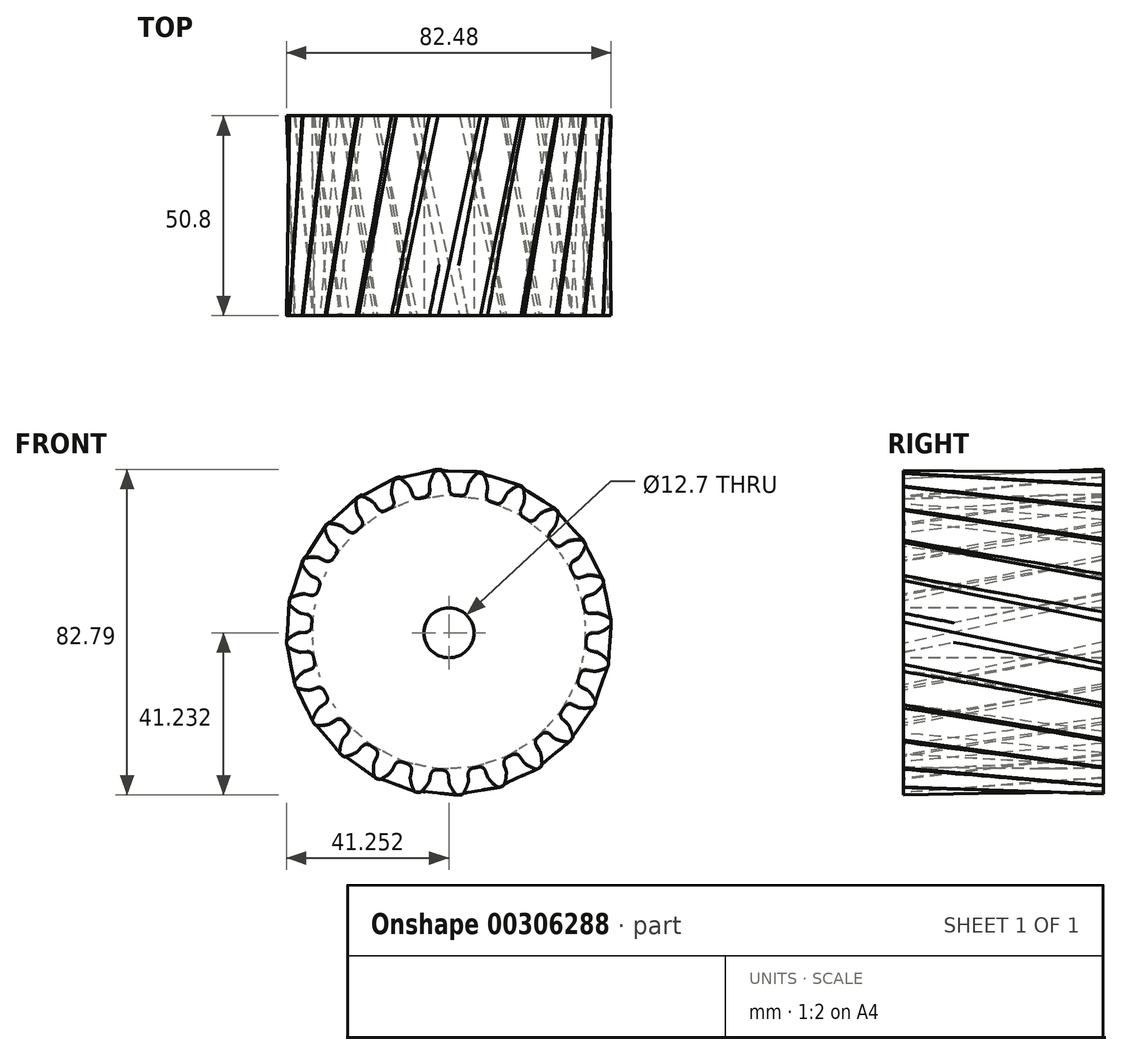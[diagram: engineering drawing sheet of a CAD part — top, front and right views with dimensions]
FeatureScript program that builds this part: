
annotation { "Feature Type Name" : "Feature", "Feature Type Description" : "" }
export const myFeature = defineFeature(function(context is Context, id is Id, definition is map)
    precondition{}
    {
        {
            var Q0;
            Q0=qCreatedBy(makeId("Front.planeOp"),FACE);
            var sketch = newSketch(context, id + "F0", { "sketchPlane" : qUnion([Q0])});
            skArc(sketch, "E0", {"start": v(-6.16, 34.38) * mm, "mid": v(-6.81, 34.25) * mm, "end": v(-7.46, 34.12) * mm});
            skArc(sketch, "E1.trimOffspring", {"start": v(-0.1, 38.36) * mm, "mid": v(-0.85, 39.78) * mm, "end": v(-1.82, 41.06) * mm});
            skLineSegment(sketch, "E2", {"start": v(0.02, 37.85) * mm, "end": v(0.11, 36.37) * mm});
            skLineSegment(sketch, "E3", {"start": v(-2.2, 41.23) * mm, "end": v(-2.7, 41.23) * mm});
            skLineSegment(sketch, "E4.MirrorCS", {"start": v(-3.2, 41.16) * mm, "end": v(-2.7, 41.23) * mm});
            skArc(sketch, "E5.MirrorCS", {"start": v(-4.9, 38.04) * mm, "mid": v(-4.35, 39.55) * mm, "end": v(-3.56, 40.95) * mm});
            skLineSegment(sketch, "E6.MirrorCS", {"start": v(-4.96, 37.52) * mm, "end": v(-4.86, 36.04) * mm});
            skPoint(sketch, "E7.orphan", {"position": v(0.33, 33.11) * mm});
            skPoint(sketch, "E8.orphan", {"position": v(-4.65, 32.79) * mm});
            skPoint(sketch, "E9.visualSharp", {"position": v(0.2, 34.92) * mm});
            skArc(sketch, "E9.filletArc", {"start": v(0.11, 36.37) * mm, "mid": v(0.59, 35.34) * mm, "end": v(1.62, 34.89) * mm});
            skPoint(sketch, "E10.visualSharp", {"position": v(-4.76, 34.6) * mm});
            skArc(sketch, "E10.filletArc", {"start": v(-6.16, 34.38) * mm, "mid": v(-5.2, 34.96) * mm, "end": v(-4.86, 36.04) * mm});
            skPoint(sketch, "E11.visualSharp", {"position": v(-3.43, 41.13) * mm});
            skArc(sketch, "E11.filletArc", {"start": v(-3.2, 41.16) * mm, "mid": v(-3.4, 41.1) * mm, "end": v(-3.56, 40.95) * mm});
            skPoint(sketch, "E12.visualSharp", {"position": v(-1.97, 41.23) * mm});
            skArc(sketch, "E12.filletArc", {"start": v(-1.82, 41.06) * mm, "mid": v(-1.99, 41.18) * mm, "end": v(-2.2, 41.23) * mm});
            skPoint(sketch, "E13.visualSharp", {"position": v(-4.97, 37.77) * mm});
            skArc(sketch, "E13.filletArc", {"start": v(-4.9, 38.04) * mm, "mid": v(-4.95, 37.78) * mm, "end": v(-4.96, 37.52) * mm});
            skPoint(sketch, "E14.visualSharp", {"position": v(0, 38.1) * mm});
            skArc(sketch, "E14.filletArc", {"start": v(0.02, 37.85) * mm, "mid": v(-0.02, 38.1) * mm, "end": v(-0.1, 38.36) * mm});
            skArc(sketch, "E15.1.0", {"start": v(-9.3, 35.16) * mm, "mid": v(-8.58, 34.29) * mm, "end": v(-7.46, 34.12) * mm});
            skArc(sketch, "E15.1.1", {"start": v(-14.85, 31.61) * mm, "mid": v(-14.07, 32.43) * mm, "end": v(-14.02, 33.56) * mm});
            skLineSegment(sketch, "E15.1.2", {"start": v(-9.78, 36.56) * mm, "end": v(-9.3, 35.16) * mm});
            skLineSegment(sketch, "E15.1.3", {"start": v(-14.5, 34.96) * mm, "end": v(-14.02, 33.56) * mm});
            skPoint(sketch, "E15.1.4", {"position": v(-12.58, 39.31) * mm});
            skPoint(sketch, "E15.1.5", {"position": v(-13.96, 38.84) * mm});
            skArc(sketch, "E15.1.6", {"start": v(-14.58, 35.48) * mm, "mid": v(-14.44, 37.08) * mm, "end": v(-14.03, 38.63) * mm});
            skPoint(sketch, "E15.1.7", {"position": v(-14.58, 35.2) * mm});
            skPoint(sketch, "E15.1.8", {"position": v(-9.86, 36.8) * mm});
            skArc(sketch, "E15.1.9", {"start": v(-10.03, 37.02) * mm, "mid": v(-11.11, 38.2) * mm, "end": v(-12.38, 39.2) * mm});
            skLineSegment(sketch, "E15.1.10", {"start": v(-12.79, 39.26) * mm, "end": v(-13.28, 39.12) * mm});
            skLineSegment(sketch, "E15.1.11", {"start": v(-13.75, 38.93) * mm, "end": v(-13.28, 39.12) * mm});
            skArc(sketch, "E15.1.12", {"start": v(-9.78, 36.56) * mm, "mid": v(-9.88, 36.8) * mm, "end": v(-10.03, 37.02) * mm});
            skArc(sketch, "E15.1.13", {"start": v(-13.75, 38.93) * mm, "mid": v(-13.92, 38.8) * mm, "end": v(-14.03, 38.63) * mm});
            skArc(sketch, "E15.1.14", {"start": v(-14.58, 35.48) * mm, "mid": v(-14.56, 35.22) * mm, "end": v(-14.5, 34.96) * mm});
            skArc(sketch, "E15.1.15", {"start": v(-12.38, 39.2) * mm, "mid": v(-12.58, 39.27) * mm, "end": v(-12.79, 39.26) * mm});
            skArc(sketch, "E15.2.0", {"start": v(-18.09, 31.55) * mm, "mid": v(-17.16, 30.9) * mm, "end": v(-16.04, 31.03) * mm});
            skArc(sketch, "E15.2.1", {"start": v(-22.53, 26.69) * mm, "mid": v(-21.98, 27.68) * mm, "end": v(-22.23, 28.78) * mm});
            skLineSegment(sketch, "E15.2.2", {"start": v(-18.9, 32.79) * mm, "end": v(-18.09, 31.55) * mm});
            skLineSegment(sketch, "E15.2.3", {"start": v(-23.05, 30.02) * mm, "end": v(-22.23, 28.78) * mm});
            skPoint(sketch, "E15.2.4", {"position": v(-22.32, 34.72) * mm});
            skPoint(sketch, "E15.2.5", {"position": v(-23.53, 33.9) * mm});
            skArc(sketch, "E15.2.6", {"start": v(-23.27, 30.5) * mm, "mid": v(-23.55, 32.08) * mm, "end": v(-23.55, 33.68) * mm});
            skPoint(sketch, "E15.2.7", {"position": v(-23.2, 30.23) * mm});
            skPoint(sketch, "E15.2.8", {"position": v(-19.05, 33) * mm});
            skArc(sketch, "E15.2.9", {"start": v(-19.27, 33.17) * mm, "mid": v(-20.62, 34.03) * mm, "end": v(-22.1, 34.65) * mm});
            skLineSegment(sketch, "E15.2.10", {"start": v(-22.51, 34.6) * mm, "end": v(-22.95, 34.35) * mm});
            skLineSegment(sketch, "E15.2.11", {"start": v(-23.36, 34.04) * mm, "end": v(-22.95, 34.35) * mm});
            skArc(sketch, "E15.2.12", {"start": v(-18.9, 32.79) * mm, "mid": v(-19.07, 33) * mm, "end": v(-19.27, 33.17) * mm});
            skArc(sketch, "E15.2.13", {"start": v(-23.36, 34.04) * mm, "mid": v(-23.5, 33.88) * mm, "end": v(-23.55, 33.68) * mm});
            skArc(sketch, "E15.2.14", {"start": v(-23.27, 30.5) * mm, "mid": v(-23.18, 30.25) * mm, "end": v(-23.05, 30.02) * mm});
            skArc(sketch, "E15.2.15", {"start": v(-22.1, 34.65) * mm, "mid": v(-22.31, 34.67) * mm, "end": v(-22.51, 34.6) * mm});
            skArc(sketch, "E15.3.0", {"start": v(-25.64, 25.8) * mm, "mid": v(-24.57, 25.4) * mm, "end": v(-23.52, 25.82) * mm});
            skArc(sketch, "E15.3.1", {"start": v(-28.67, 19.95) * mm, "mid": v(-28.4, 21.05) * mm, "end": v(-28.92, 22.05) * mm});
            skLineSegment(sketch, "E15.3.2", {"start": v(-26.75, 26.77) * mm, "end": v(-25.64, 25.8) * mm});
            skLineSegment(sketch, "E15.3.3", {"start": v(-30.04, 23.03) * mm, "end": v(-28.92, 22.05) * mm});
            skPoint(sketch, "E15.3.4", {"position": v(-30.55, 27.76) * mm});
            skPoint(sketch, "E15.3.5", {"position": v(-31.5, 26.66) * mm});
            skArc(sketch, "E15.3.6", {"start": v(-30.37, 23.43) * mm, "mid": v(-31.05, 24.89) * mm, "end": v(-31.47, 26.44) * mm});
            skPoint(sketch, "E15.3.7", {"position": v(-30.23, 23.2) * mm});
            skPoint(sketch, "E15.3.8", {"position": v(-26.94, 26.94) * mm});
            skArc(sketch, "E15.3.9", {"start": v(-27.2, 27.05) * mm, "mid": v(-28.73, 27.53) * mm, "end": v(-30.32, 27.75) * mm});
            skLineSegment(sketch, "E15.3.10", {"start": v(-30.7, 27.6) * mm, "end": v(-31.06, 27.24) * mm});
            skLineSegment(sketch, "E15.3.11", {"start": v(-31.37, 26.84) * mm, "end": v(-31.06, 27.24) * mm});
            skArc(sketch, "E15.3.12", {"start": v(-26.75, 26.77) * mm, "mid": v(-26.96, 26.93) * mm, "end": v(-27.2, 27.05) * mm});
            skArc(sketch, "E15.3.13", {"start": v(-31.37, 26.84) * mm, "mid": v(-31.46, 26.65) * mm, "end": v(-31.47, 26.44) * mm});
            skArc(sketch, "E15.3.14", {"start": v(-30.37, 23.43) * mm, "mid": v(-30.22, 23.22) * mm, "end": v(-30.04, 23.03) * mm});
            skArc(sketch, "E15.3.15", {"start": v(-30.32, 27.75) * mm, "mid": v(-30.53, 27.72) * mm, "end": v(-30.7, 27.6) * mm});
            skArc(sketch, "E15.4.0", {"start": v(-31.44, 18.28) * mm, "mid": v(-30.31, 18.18) * mm, "end": v(-29.4, 18.85) * mm});
            skArc(sketch, "E15.4.1", {"start": v(-32.85, 11.85) * mm, "mid": v(-32.87, 12.98) * mm, "end": v(-33.64, 13.81) * mm});
            skLineSegment(sketch, "E15.4.2", {"start": v(-32.77, 18.94) * mm, "end": v(-31.44, 18.28) * mm});
            skLineSegment(sketch, "E15.4.3", {"start": v(-34.97, 14.47) * mm, "end": v(-33.64, 13.81) * mm});
            skPoint(sketch, "E15.4.4", {"position": v(-36.7, 18.9) * mm});
            skPoint(sketch, "E15.4.5", {"position": v(-37.33, 17.6) * mm});
            skArc(sketch, "E15.4.6", {"start": v(-35.4, 14.77) * mm, "mid": v(-36.43, 16) * mm, "end": v(-37.24, 17.4) * mm});
            skPoint(sketch, "E15.4.7", {"position": v(-35.2, 14.58) * mm});
            skPoint(sketch, "E15.4.8", {"position": v(-33, 19.05) * mm});
            skArc(sketch, "E15.4.9", {"start": v(-33.27, 19.09) * mm, "mid": v(-34.87, 19.16) * mm, "end": v(-36.47, 18.96) * mm});
            skLineSegment(sketch, "E15.4.10", {"start": v(-36.8, 18.71) * mm, "end": v(-37.06, 18.27) * mm});
            skLineSegment(sketch, "E15.4.11", {"start": v(-37.25, 17.8) * mm, "end": v(-37.06, 18.27) * mm});
            skArc(sketch, "E15.4.12", {"start": v(-32.77, 18.94) * mm, "mid": v(-33.01, 19.03) * mm, "end": v(-33.27, 19.09) * mm});
            skArc(sketch, "E15.4.13", {"start": v(-37.25, 17.8) * mm, "mid": v(-37.29, 17.6) * mm, "end": v(-37.24, 17.4) * mm});
            skArc(sketch, "E15.4.14", {"start": v(-35.4, 14.77) * mm, "mid": v(-35.2, 14.6) * mm, "end": v(-34.97, 14.47) * mm});
            skArc(sketch, "E15.4.15", {"start": v(-36.47, 18.96) * mm, "mid": v(-36.66, 18.87) * mm, "end": v(-36.8, 18.71) * mm});
            skArc(sketch, "E15.5.0", {"start": v(-35.1, 9.52) * mm, "mid": v(-33.98, 9.71) * mm, "end": v(-33.28, 10.6) * mm});
            skArc(sketch, "E15.5.1", {"start": v(-34.8, 2.94) * mm, "mid": v(-35.11, 4.03) * mm, "end": v(-36.07, 4.63) * mm});
            skLineSegment(sketch, "E15.5.2", {"start": v(-36.55, 9.81) * mm, "end": v(-35.1, 9.52) * mm});
            skLineSegment(sketch, "E15.5.3", {"start": v(-37.53, 4.92) * mm, "end": v(-36.07, 4.63) * mm});
            skPoint(sketch, "E15.5.4", {"position": v(-40.33, 8.77) * mm});
            skPoint(sketch, "E15.5.5", {"position": v(-40.62, 7.34) * mm});
            skArc(sketch, "E15.5.6", {"start": v(-38.02, 5.1) * mm, "mid": v(-39.33, 6.03) * mm, "end": v(-40.47, 7.16) * mm});
            skPoint(sketch, "E15.5.7", {"position": v(-37.77, 4.97) * mm});
            skPoint(sketch, "E15.5.8", {"position": v(-36.8, 9.86) * mm});
            skArc(sketch, "E15.5.9", {"start": v(-37.08, 9.83) * mm, "mid": v(-38.64, 9.48) * mm, "end": v(-40.13, 8.87) * mm});
            skLineSegment(sketch, "E15.5.10", {"start": v(-40.4, 8.55) * mm, "end": v(-40.52, 8.06) * mm});
            skLineSegment(sketch, "E15.5.11", {"start": v(-40.59, 7.56) * mm, "end": v(-40.52, 8.06) * mm});
            skArc(sketch, "E15.5.12", {"start": v(-36.55, 9.81) * mm, "mid": v(-36.81, 9.84) * mm, "end": v(-37.08, 9.83) * mm});
            skArc(sketch, "E15.5.13", {"start": v(-40.59, 7.56) * mm, "mid": v(-40.57, 7.35) * mm, "end": v(-40.47, 7.16) * mm});
            skArc(sketch, "E15.5.14", {"start": v(-38.02, 5.1) * mm, "mid": v(-37.78, 5) * mm, "end": v(-37.53, 4.92) * mm});
            skArc(sketch, "E15.5.15", {"start": v(-40.13, 8.87) * mm, "mid": v(-40.3, 8.74) * mm, "end": v(-40.4, 8.55) * mm});
            skArc(sketch, "E15.6.0", {"start": v(-36.37, 0.11) * mm, "mid": v(-35.34, 0.59) * mm, "end": v(-34.89, 1.62) * mm});
            skArc(sketch, "E15.6.1", {"start": v(-34.38, -6.16) * mm, "mid": v(-34.96, -5.2) * mm, "end": v(-36.04, -4.86) * mm});
            skLineSegment(sketch, "E15.6.2", {"start": v(-37.85, 0.02) * mm, "end": v(-36.37, 0.11) * mm});
            skLineSegment(sketch, "E15.6.3", {"start": v(-37.52, -4.96) * mm, "end": v(-36.04, -4.86) * mm});
            skPoint(sketch, "E15.6.4", {"position": v(-41.23, -1.97) * mm});
            skPoint(sketch, "E15.6.5", {"position": v(-41.13, -3.43) * mm});
            skArc(sketch, "E15.6.6", {"start": v(-38.04, -4.9) * mm, "mid": v(-39.55, -4.35) * mm, "end": v(-40.95, -3.56) * mm});
            skPoint(sketch, "E15.6.7", {"position": v(-37.77, -4.97) * mm});
            skPoint(sketch, "E15.6.8", {"position": v(-38.1, 0) * mm});
            skArc(sketch, "E15.6.9", {"start": v(-38.36, -0.1) * mm, "mid": v(-39.78, -0.85) * mm, "end": v(-41.06, -1.82) * mm});
            skLineSegment(sketch, "E15.6.10", {"start": v(-41.23, -2.2) * mm, "end": v(-41.23, -2.7) * mm});
            skLineSegment(sketch, "E15.6.11", {"start": v(-41.16, -3.2) * mm, "end": v(-41.23, -2.7) * mm});
            skArc(sketch, "E15.6.12", {"start": v(-37.85, 0.02) * mm, "mid": v(-38.1, -0.02) * mm, "end": v(-38.36, -0.1) * mm});
            skArc(sketch, "E15.6.13", {"start": v(-41.16, -3.2) * mm, "mid": v(-41.1, -3.4) * mm, "end": v(-40.95, -3.56) * mm});
            skArc(sketch, "E15.6.14", {"start": v(-38.04, -4.9) * mm, "mid": v(-37.78, -4.95) * mm, "end": v(-37.52, -4.96) * mm});
            skArc(sketch, "E15.6.15", {"start": v(-41.06, -1.82) * mm, "mid": v(-41.18, -1.99) * mm, "end": v(-41.23, -2.2) * mm});
            skArc(sketch, "E15.7.0", {"start": v(-35.16, -9.3) * mm, "mid": v(-34.29, -8.58) * mm, "end": v(-34.12, -7.46) * mm});
            skArc(sketch, "E15.7.1", {"start": v(-31.61, -14.85) * mm, "mid": v(-32.43, -14.07) * mm, "end": v(-33.56, -14.02) * mm});
            skLineSegment(sketch, "E15.7.2", {"start": v(-36.56, -9.78) * mm, "end": v(-35.16, -9.3) * mm});
            skLineSegment(sketch, "E15.7.3", {"start": v(-34.96, -14.5) * mm, "end": v(-33.56, -14.02) * mm});
            skPoint(sketch, "E15.7.4", {"position": v(-39.31, -12.58) * mm});
            skPoint(sketch, "E15.7.5", {"position": v(-38.84, -13.96) * mm});
            skArc(sketch, "E15.7.6", {"start": v(-35.48, -14.58) * mm, "mid": v(-37.08, -14.44) * mm, "end": v(-38.63, -14.03) * mm});
            skPoint(sketch, "E15.7.7", {"position": v(-35.2, -14.58) * mm});
            skPoint(sketch, "E15.7.8", {"position": v(-36.8, -9.86) * mm});
            skArc(sketch, "E15.7.9", {"start": v(-37.02, -10.03) * mm, "mid": v(-38.2, -11.11) * mm, "end": v(-39.2, -12.38) * mm});
            skLineSegment(sketch, "E15.7.10", {"start": v(-39.26, -12.79) * mm, "end": v(-39.12, -13.28) * mm});
            skLineSegment(sketch, "E15.7.11", {"start": v(-38.93, -13.75) * mm, "end": v(-39.12, -13.28) * mm});
            skArc(sketch, "E15.7.12", {"start": v(-36.56, -9.78) * mm, "mid": v(-36.8, -9.88) * mm, "end": v(-37.02, -10.03) * mm});
            skArc(sketch, "E15.7.13", {"start": v(-38.93, -13.75) * mm, "mid": v(-38.8, -13.92) * mm, "end": v(-38.63, -14.03) * mm});
            skArc(sketch, "E15.7.14", {"start": v(-35.48, -14.58) * mm, "mid": v(-35.22, -14.56) * mm, "end": v(-34.96, -14.5) * mm});
            skArc(sketch, "E15.7.15", {"start": v(-39.2, -12.38) * mm, "mid": v(-39.27, -12.58) * mm, "end": v(-39.26, -12.79) * mm});
            skArc(sketch, "E15.8.0", {"start": v(-31.55, -18.09) * mm, "mid": v(-30.9, -17.16) * mm, "end": v(-31.03, -16.04) * mm});
            skArc(sketch, "E15.8.1", {"start": v(-26.69, -22.53) * mm, "mid": v(-27.68, -21.98) * mm, "end": v(-28.78, -22.23) * mm});
            skLineSegment(sketch, "E15.8.2", {"start": v(-32.79, -18.9) * mm, "end": v(-31.55, -18.09) * mm});
            skLineSegment(sketch, "E15.8.3", {"start": v(-30.02, -23.05) * mm, "end": v(-28.78, -22.23) * mm});
            skPoint(sketch, "E15.8.4", {"position": v(-34.72, -22.32) * mm});
            skPoint(sketch, "E15.8.5", {"position": v(-33.9, -23.53) * mm});
            skArc(sketch, "E15.8.6", {"start": v(-30.5, -23.27) * mm, "mid": v(-32.08, -23.55) * mm, "end": v(-33.68, -23.55) * mm});
            skPoint(sketch, "E15.8.7", {"position": v(-30.23, -23.2) * mm});
            skPoint(sketch, "E15.8.8", {"position": v(-33, -19.05) * mm});
            skArc(sketch, "E15.8.9", {"start": v(-33.17, -19.27) * mm, "mid": v(-34.03, -20.62) * mm, "end": v(-34.65, -22.1) * mm});
            skLineSegment(sketch, "E15.8.10", {"start": v(-34.6, -22.51) * mm, "end": v(-34.35, -22.95) * mm});
            skLineSegment(sketch, "E15.8.11", {"start": v(-34.04, -23.36) * mm, "end": v(-34.35, -22.95) * mm});
            skArc(sketch, "E15.8.12", {"start": v(-32.79, -18.9) * mm, "mid": v(-33, -19.07) * mm, "end": v(-33.17, -19.27) * mm});
            skArc(sketch, "E15.8.13", {"start": v(-34.04, -23.36) * mm, "mid": v(-33.88, -23.5) * mm, "end": v(-33.68, -23.55) * mm});
            skArc(sketch, "E15.8.14", {"start": v(-30.5, -23.27) * mm, "mid": v(-30.25, -23.18) * mm, "end": v(-30.02, -23.05) * mm});
            skArc(sketch, "E15.8.15", {"start": v(-34.65, -22.1) * mm, "mid": v(-34.67, -22.31) * mm, "end": v(-34.6, -22.51) * mm});
            skArc(sketch, "E15.9.0", {"start": v(-25.8, -25.64) * mm, "mid": v(-25.4, -24.57) * mm, "end": v(-25.82, -23.52) * mm});
            skArc(sketch, "E15.9.1", {"start": v(-19.95, -28.67) * mm, "mid": v(-21.05, -28.4) * mm, "end": v(-22.05, -28.92) * mm});
            skLineSegment(sketch, "E15.9.2", {"start": v(-26.77, -26.75) * mm, "end": v(-25.8, -25.64) * mm});
            skLineSegment(sketch, "E15.9.3", {"start": v(-23.03, -30.04) * mm, "end": v(-22.05, -28.92) * mm});
            skPoint(sketch, "E15.9.4", {"position": v(-27.76, -30.55) * mm});
            skPoint(sketch, "E15.9.5", {"position": v(-26.66, -31.5) * mm});
            skArc(sketch, "E15.9.6", {"start": v(-23.43, -30.37) * mm, "mid": v(-24.89, -31.05) * mm, "end": v(-26.44, -31.47) * mm});
            skPoint(sketch, "E15.9.7", {"position": v(-23.2, -30.23) * mm});
            skPoint(sketch, "E15.9.8", {"position": v(-26.94, -26.94) * mm});
            skArc(sketch, "E15.9.9", {"start": v(-27.05, -27.2) * mm, "mid": v(-27.53, -28.73) * mm, "end": v(-27.75, -30.32) * mm});
            skLineSegment(sketch, "E15.9.10", {"start": v(-27.6, -30.7) * mm, "end": v(-27.24, -31.06) * mm});
            skLineSegment(sketch, "E15.9.11", {"start": v(-26.84, -31.37) * mm, "end": v(-27.24, -31.06) * mm});
            skArc(sketch, "E15.9.12", {"start": v(-26.77, -26.75) * mm, "mid": v(-26.93, -26.96) * mm, "end": v(-27.05, -27.2) * mm});
            skArc(sketch, "E15.9.13", {"start": v(-26.84, -31.37) * mm, "mid": v(-26.65, -31.46) * mm, "end": v(-26.44, -31.47) * mm});
            skArc(sketch, "E15.9.14", {"start": v(-23.43, -30.37) * mm, "mid": v(-23.22, -30.22) * mm, "end": v(-23.03, -30.04) * mm});
            skArc(sketch, "E15.9.15", {"start": v(-27.75, -30.32) * mm, "mid": v(-27.72, -30.53) * mm, "end": v(-27.6, -30.7) * mm});
            skArc(sketch, "E15.10.0", {"start": v(-18.28, -31.44) * mm, "mid": v(-18.18, -30.31) * mm, "end": v(-18.85, -29.4) * mm});
            skArc(sketch, "E15.10.1", {"start": v(-11.85, -32.85) * mm, "mid": v(-12.98, -32.87) * mm, "end": v(-13.81, -33.64) * mm});
            skLineSegment(sketch, "E15.10.2", {"start": v(-18.94, -32.77) * mm, "end": v(-18.28, -31.44) * mm});
            skLineSegment(sketch, "E15.10.3", {"start": v(-14.47, -34.97) * mm, "end": v(-13.81, -33.64) * mm});
            skPoint(sketch, "E15.10.4", {"position": v(-18.9, -36.7) * mm});
            skPoint(sketch, "E15.10.5", {"position": v(-17.6, -37.33) * mm});
            skArc(sketch, "E15.10.6", {"start": v(-14.77, -35.4) * mm, "mid": v(-16, -36.43) * mm, "end": v(-17.4, -37.24) * mm});
            skPoint(sketch, "E15.10.7", {"position": v(-14.58, -35.2) * mm});
            skPoint(sketch, "E15.10.8", {"position": v(-19.05, -33) * mm});
            skArc(sketch, "E15.10.9", {"start": v(-19.09, -33.27) * mm, "mid": v(-19.16, -34.87) * mm, "end": v(-18.96, -36.47) * mm});
            skLineSegment(sketch, "E15.10.10", {"start": v(-18.71, -36.8) * mm, "end": v(-18.27, -37.06) * mm});
            skLineSegment(sketch, "E15.10.11", {"start": v(-17.8, -37.25) * mm, "end": v(-18.27, -37.06) * mm});
            skArc(sketch, "E15.10.12", {"start": v(-18.94, -32.77) * mm, "mid": v(-19.03, -33.01) * mm, "end": v(-19.09, -33.27) * mm});
            skArc(sketch, "E15.10.13", {"start": v(-17.8, -37.25) * mm, "mid": v(-17.6, -37.29) * mm, "end": v(-17.4, -37.24) * mm});
            skArc(sketch, "E15.10.14", {"start": v(-14.77, -35.4) * mm, "mid": v(-14.6, -35.2) * mm, "end": v(-14.47, -34.97) * mm});
            skArc(sketch, "E15.10.15", {"start": v(-18.96, -36.47) * mm, "mid": v(-18.87, -36.66) * mm, "end": v(-18.71, -36.8) * mm});
            skArc(sketch, "E15.11.0", {"start": v(-9.52, -35.1) * mm, "mid": v(-9.71, -33.98) * mm, "end": v(-10.6, -33.28) * mm});
            skArc(sketch, "E15.11.1", {"start": v(-2.94, -34.8) * mm, "mid": v(-4.03, -35.11) * mm, "end": v(-4.63, -36.07) * mm});
            skLineSegment(sketch, "E15.11.2", {"start": v(-9.81, -36.55) * mm, "end": v(-9.52, -35.1) * mm});
            skLineSegment(sketch, "E15.11.3", {"start": v(-4.92, -37.53) * mm, "end": v(-4.63, -36.07) * mm});
            skPoint(sketch, "E15.11.4", {"position": v(-8.77, -40.33) * mm});
            skPoint(sketch, "E15.11.5", {"position": v(-7.34, -40.62) * mm});
            skArc(sketch, "E15.11.6", {"start": v(-5.1, -38.02) * mm, "mid": v(-6.03, -39.33) * mm, "end": v(-7.16, -40.47) * mm});
            skPoint(sketch, "E15.11.7", {"position": v(-4.97, -37.77) * mm});
            skPoint(sketch, "E15.11.8", {"position": v(-9.86, -36.8) * mm});
            skArc(sketch, "E15.11.9", {"start": v(-9.83, -37.08) * mm, "mid": v(-9.48, -38.64) * mm, "end": v(-8.87, -40.13) * mm});
            skLineSegment(sketch, "E15.11.10", {"start": v(-8.55, -40.4) * mm, "end": v(-8.06, -40.52) * mm});
            skLineSegment(sketch, "E15.11.11", {"start": v(-7.56, -40.59) * mm, "end": v(-8.06, -40.52) * mm});
            skArc(sketch, "E15.11.12", {"start": v(-9.81, -36.55) * mm, "mid": v(-9.84, -36.81) * mm, "end": v(-9.83, -37.08) * mm});
            skArc(sketch, "E15.11.13", {"start": v(-7.56, -40.59) * mm, "mid": v(-7.35, -40.57) * mm, "end": v(-7.16, -40.47) * mm});
            skArc(sketch, "E15.11.14", {"start": v(-5.1, -38.02) * mm, "mid": v(-5, -37.78) * mm, "end": v(-4.92, -37.53) * mm});
            skArc(sketch, "E15.11.15", {"start": v(-8.87, -40.13) * mm, "mid": v(-8.74, -40.3) * mm, "end": v(-8.55, -40.4) * mm});
            skArc(sketch, "E15.12.0", {"start": v(-0.11, -36.37) * mm, "mid": v(-0.59, -35.34) * mm, "end": v(-1.62, -34.89) * mm});
            skArc(sketch, "E15.12.1", {"start": v(6.16, -34.38) * mm, "mid": v(5.2, -34.96) * mm, "end": v(4.86, -36.04) * mm});
            skLineSegment(sketch, "E15.12.2", {"start": v(-0.02, -37.85) * mm, "end": v(-0.11, -36.37) * mm});
            skLineSegment(sketch, "E15.12.3", {"start": v(4.96, -37.52) * mm, "end": v(4.86, -36.04) * mm});
            skPoint(sketch, "E15.12.4", {"position": v(1.97, -41.23) * mm});
            skPoint(sketch, "E15.12.5", {"position": v(3.43, -41.13) * mm});
            skArc(sketch, "E15.12.6", {"start": v(4.9, -38.04) * mm, "mid": v(4.35, -39.55) * mm, "end": v(3.56, -40.95) * mm});
            skPoint(sketch, "E15.12.7", {"position": v(4.97, -37.77) * mm});
            skPoint(sketch, "E15.12.8", {"position": v(0, -38.1) * mm});
            skArc(sketch, "E15.12.9", {"start": v(0.1, -38.36) * mm, "mid": v(0.85, -39.78) * mm, "end": v(1.82, -41.06) * mm});
            skLineSegment(sketch, "E15.12.10", {"start": v(2.2, -41.23) * mm, "end": v(2.7, -41.23) * mm});
            skLineSegment(sketch, "E15.12.11", {"start": v(3.2, -41.16) * mm, "end": v(2.7, -41.23) * mm});
            skArc(sketch, "E15.12.12", {"start": v(-0.02, -37.85) * mm, "mid": v(0.02, -38.1) * mm, "end": v(0.1, -38.36) * mm});
            skArc(sketch, "E15.12.13", {"start": v(3.2, -41.16) * mm, "mid": v(3.4, -41.1) * mm, "end": v(3.56, -40.95) * mm});
            skArc(sketch, "E15.12.14", {"start": v(4.9, -38.04) * mm, "mid": v(4.95, -37.78) * mm, "end": v(4.96, -37.52) * mm});
            skArc(sketch, "E15.12.15", {"start": v(1.82, -41.06) * mm, "mid": v(1.99, -41.18) * mm, "end": v(2.2, -41.23) * mm});
            skArc(sketch, "E15.13.0", {"start": v(9.3, -35.16) * mm, "mid": v(8.58, -34.29) * mm, "end": v(7.46, -34.12) * mm});
            skArc(sketch, "E15.13.1", {"start": v(14.85, -31.61) * mm, "mid": v(14.07, -32.43) * mm, "end": v(14.02, -33.56) * mm});
            skLineSegment(sketch, "E15.13.2", {"start": v(9.78, -36.56) * mm, "end": v(9.3, -35.16) * mm});
            skLineSegment(sketch, "E15.13.3", {"start": v(14.5, -34.96) * mm, "end": v(14.02, -33.56) * mm});
            skPoint(sketch, "E15.13.4", {"position": v(12.58, -39.31) * mm});
            skPoint(sketch, "E15.13.5", {"position": v(13.96, -38.84) * mm});
            skArc(sketch, "E15.13.6", {"start": v(14.58, -35.48) * mm, "mid": v(14.44, -37.08) * mm, "end": v(14.03, -38.63) * mm});
            skPoint(sketch, "E15.13.7", {"position": v(14.58, -35.2) * mm});
            skPoint(sketch, "E15.13.8", {"position": v(9.86, -36.8) * mm});
            skArc(sketch, "E15.13.9", {"start": v(10.03, -37.02) * mm, "mid": v(11.11, -38.2) * mm, "end": v(12.38, -39.2) * mm});
            skLineSegment(sketch, "E15.13.10", {"start": v(12.79, -39.26) * mm, "end": v(13.28, -39.12) * mm});
            skLineSegment(sketch, "E15.13.11", {"start": v(13.75, -38.93) * mm, "end": v(13.28, -39.12) * mm});
            skArc(sketch, "E15.13.12", {"start": v(9.78, -36.56) * mm, "mid": v(9.88, -36.8) * mm, "end": v(10.03, -37.02) * mm});
            skArc(sketch, "E15.13.13", {"start": v(13.75, -38.93) * mm, "mid": v(13.92, -38.8) * mm, "end": v(14.03, -38.63) * mm});
            skArc(sketch, "E15.13.14", {"start": v(14.58, -35.48) * mm, "mid": v(14.56, -35.22) * mm, "end": v(14.5, -34.96) * mm});
            skArc(sketch, "E15.13.15", {"start": v(12.38, -39.2) * mm, "mid": v(12.58, -39.27) * mm, "end": v(12.79, -39.26) * mm});
            skArc(sketch, "E15.14.0", {"start": v(18.09, -31.55) * mm, "mid": v(17.16, -30.9) * mm, "end": v(16.04, -31.03) * mm});
            skArc(sketch, "E15.14.1", {"start": v(22.53, -26.69) * mm, "mid": v(21.98, -27.68) * mm, "end": v(22.23, -28.78) * mm});
            skLineSegment(sketch, "E15.14.2", {"start": v(18.9, -32.79) * mm, "end": v(18.09, -31.55) * mm});
            skLineSegment(sketch, "E15.14.3", {"start": v(23.05, -30.02) * mm, "end": v(22.23, -28.78) * mm});
            skPoint(sketch, "E15.14.4", {"position": v(22.32, -34.72) * mm});
            skPoint(sketch, "E15.14.5", {"position": v(23.53, -33.9) * mm});
            skArc(sketch, "E15.14.6", {"start": v(23.27, -30.5) * mm, "mid": v(23.55, -32.08) * mm, "end": v(23.55, -33.68) * mm});
            skPoint(sketch, "E15.14.7", {"position": v(23.2, -30.23) * mm});
            skPoint(sketch, "E15.14.8", {"position": v(19.05, -33) * mm});
            skArc(sketch, "E15.14.9", {"start": v(19.27, -33.17) * mm, "mid": v(20.62, -34.03) * mm, "end": v(22.1, -34.65) * mm});
            skLineSegment(sketch, "E15.14.10", {"start": v(22.51, -34.6) * mm, "end": v(22.95, -34.35) * mm});
            skLineSegment(sketch, "E15.14.11", {"start": v(23.36, -34.04) * mm, "end": v(22.95, -34.35) * mm});
            skArc(sketch, "E15.14.12", {"start": v(18.9, -32.79) * mm, "mid": v(19.07, -33) * mm, "end": v(19.27, -33.17) * mm});
            skArc(sketch, "E15.14.13", {"start": v(23.36, -34.04) * mm, "mid": v(23.5, -33.88) * mm, "end": v(23.55, -33.68) * mm});
            skArc(sketch, "E15.14.14", {"start": v(23.27, -30.5) * mm, "mid": v(23.18, -30.25) * mm, "end": v(23.05, -30.02) * mm});
            skArc(sketch, "E15.14.15", {"start": v(22.1, -34.65) * mm, "mid": v(22.31, -34.67) * mm, "end": v(22.51, -34.6) * mm});
            skArc(sketch, "E15.15.0", {"start": v(25.64, -25.8) * mm, "mid": v(24.57, -25.4) * mm, "end": v(23.52, -25.82) * mm});
            skArc(sketch, "E15.15.1", {"start": v(28.67, -19.95) * mm, "mid": v(28.4, -21.05) * mm, "end": v(28.92, -22.05) * mm});
            skLineSegment(sketch, "E15.15.2", {"start": v(26.75, -26.77) * mm, "end": v(25.64, -25.8) * mm});
            skLineSegment(sketch, "E15.15.3", {"start": v(30.04, -23.03) * mm, "end": v(28.92, -22.05) * mm});
            skPoint(sketch, "E15.15.4", {"position": v(30.55, -27.76) * mm});
            skPoint(sketch, "E15.15.5", {"position": v(31.5, -26.66) * mm});
            skArc(sketch, "E15.15.6", {"start": v(30.37, -23.43) * mm, "mid": v(31.05, -24.89) * mm, "end": v(31.47, -26.44) * mm});
            skPoint(sketch, "E15.15.7", {"position": v(30.23, -23.2) * mm});
            skPoint(sketch, "E15.15.8", {"position": v(26.94, -26.94) * mm});
            skArc(sketch, "E15.15.9", {"start": v(27.2, -27.05) * mm, "mid": v(28.73, -27.53) * mm, "end": v(30.32, -27.75) * mm});
            skLineSegment(sketch, "E15.15.10", {"start": v(30.7, -27.6) * mm, "end": v(31.06, -27.24) * mm});
            skLineSegment(sketch, "E15.15.11", {"start": v(31.37, -26.84) * mm, "end": v(31.06, -27.24) * mm});
            skArc(sketch, "E15.15.12", {"start": v(26.75, -26.77) * mm, "mid": v(26.96, -26.93) * mm, "end": v(27.2, -27.05) * mm});
            skArc(sketch, "E15.15.13", {"start": v(31.37, -26.84) * mm, "mid": v(31.46, -26.65) * mm, "end": v(31.47, -26.44) * mm});
            skArc(sketch, "E15.15.14", {"start": v(30.37, -23.43) * mm, "mid": v(30.22, -23.22) * mm, "end": v(30.04, -23.03) * mm});
            skArc(sketch, "E15.15.15", {"start": v(30.32, -27.75) * mm, "mid": v(30.53, -27.72) * mm, "end": v(30.7, -27.6) * mm});
            skArc(sketch, "E15.16.0", {"start": v(31.44, -18.28) * mm, "mid": v(30.31, -18.18) * mm, "end": v(29.4, -18.85) * mm});
            skArc(sketch, "E15.16.1", {"start": v(32.85, -11.85) * mm, "mid": v(32.87, -12.98) * mm, "end": v(33.64, -13.81) * mm});
            skLineSegment(sketch, "E15.16.2", {"start": v(32.77, -18.94) * mm, "end": v(31.44, -18.28) * mm});
            skLineSegment(sketch, "E15.16.3", {"start": v(34.97, -14.47) * mm, "end": v(33.64, -13.81) * mm});
            skPoint(sketch, "E15.16.4", {"position": v(36.7, -18.9) * mm});
            skPoint(sketch, "E15.16.5", {"position": v(37.33, -17.6) * mm});
            skArc(sketch, "E15.16.6", {"start": v(35.4, -14.77) * mm, "mid": v(36.43, -16) * mm, "end": v(37.24, -17.4) * mm});
            skPoint(sketch, "E15.16.7", {"position": v(35.2, -14.58) * mm});
            skPoint(sketch, "E15.16.8", {"position": v(33, -19.05) * mm});
            skArc(sketch, "E15.16.9", {"start": v(33.27, -19.09) * mm, "mid": v(34.87, -19.16) * mm, "end": v(36.47, -18.96) * mm});
            skLineSegment(sketch, "E15.16.10", {"start": v(36.8, -18.71) * mm, "end": v(37.06, -18.27) * mm});
            skLineSegment(sketch, "E15.16.11", {"start": v(37.25, -17.8) * mm, "end": v(37.06, -18.27) * mm});
            skArc(sketch, "E15.16.12", {"start": v(32.77, -18.94) * mm, "mid": v(33.01, -19.03) * mm, "end": v(33.27, -19.09) * mm});
            skArc(sketch, "E15.16.13", {"start": v(37.25, -17.8) * mm, "mid": v(37.29, -17.6) * mm, "end": v(37.24, -17.4) * mm});
            skArc(sketch, "E15.16.14", {"start": v(35.4, -14.77) * mm, "mid": v(35.2, -14.6) * mm, "end": v(34.97, -14.47) * mm});
            skArc(sketch, "E15.16.15", {"start": v(36.47, -18.96) * mm, "mid": v(36.66, -18.87) * mm, "end": v(36.8, -18.71) * mm});
            skArc(sketch, "E15.17.0", {"start": v(35.1, -9.52) * mm, "mid": v(33.98, -9.71) * mm, "end": v(33.28, -10.6) * mm});
            skArc(sketch, "E15.17.1", {"start": v(34.8, -2.94) * mm, "mid": v(35.11, -4.03) * mm, "end": v(36.07, -4.63) * mm});
            skLineSegment(sketch, "E15.17.2", {"start": v(36.55, -9.81) * mm, "end": v(35.1, -9.52) * mm});
            skLineSegment(sketch, "E15.17.3", {"start": v(37.53, -4.92) * mm, "end": v(36.07, -4.63) * mm});
            skPoint(sketch, "E15.17.4", {"position": v(40.33, -8.77) * mm});
            skPoint(sketch, "E15.17.5", {"position": v(40.62, -7.34) * mm});
            skArc(sketch, "E15.17.6", {"start": v(38.02, -5.1) * mm, "mid": v(39.33, -6.03) * mm, "end": v(40.47, -7.16) * mm});
            skPoint(sketch, "E15.17.7", {"position": v(37.77, -4.97) * mm});
            skPoint(sketch, "E15.17.8", {"position": v(36.8, -9.86) * mm});
            skArc(sketch, "E15.17.9", {"start": v(37.08, -9.83) * mm, "mid": v(38.64, -9.48) * mm, "end": v(40.13, -8.87) * mm});
            skLineSegment(sketch, "E15.17.10", {"start": v(40.4, -8.55) * mm, "end": v(40.52, -8.06) * mm});
            skLineSegment(sketch, "E15.17.11", {"start": v(40.59, -7.56) * mm, "end": v(40.52, -8.06) * mm});
            skArc(sketch, "E15.17.12", {"start": v(36.55, -9.81) * mm, "mid": v(36.81, -9.84) * mm, "end": v(37.08, -9.83) * mm});
            skArc(sketch, "E15.17.13", {"start": v(40.59, -7.56) * mm, "mid": v(40.57, -7.35) * mm, "end": v(40.47, -7.16) * mm});
            skArc(sketch, "E15.17.14", {"start": v(38.02, -5.1) * mm, "mid": v(37.78, -5) * mm, "end": v(37.53, -4.92) * mm});
            skArc(sketch, "E15.17.15", {"start": v(40.13, -8.87) * mm, "mid": v(40.3, -8.74) * mm, "end": v(40.4, -8.55) * mm});
            skArc(sketch, "E15.18.0", {"start": v(36.37, -0.11) * mm, "mid": v(35.34, -0.59) * mm, "end": v(34.89, -1.62) * mm});
            skArc(sketch, "E15.18.1", {"start": v(34.38, 6.16) * mm, "mid": v(34.96, 5.2) * mm, "end": v(36.04, 4.86) * mm});
            skLineSegment(sketch, "E15.18.2", {"start": v(37.85, -0.02) * mm, "end": v(36.37, -0.11) * mm});
            skLineSegment(sketch, "E15.18.3", {"start": v(37.52, 4.96) * mm, "end": v(36.04, 4.86) * mm});
            skPoint(sketch, "E15.18.4", {"position": v(41.23, 1.97) * mm});
            skPoint(sketch, "E15.18.5", {"position": v(41.13, 3.43) * mm});
            skArc(sketch, "E15.18.6", {"start": v(38.04, 4.9) * mm, "mid": v(39.55, 4.35) * mm, "end": v(40.95, 3.56) * mm});
            skPoint(sketch, "E15.18.7", {"position": v(37.77, 4.97) * mm});
            skPoint(sketch, "E15.18.8", {"position": v(38.1, 0) * mm});
            skArc(sketch, "E15.18.9", {"start": v(38.36, 0.1) * mm, "mid": v(39.78, 0.85) * mm, "end": v(41.06, 1.82) * mm});
            skLineSegment(sketch, "E15.18.10", {"start": v(41.23, 2.2) * mm, "end": v(41.23, 2.7) * mm});
            skLineSegment(sketch, "E15.18.11", {"start": v(41.16, 3.2) * mm, "end": v(41.23, 2.7) * mm});
            skArc(sketch, "E15.18.12", {"start": v(37.85, -0.02) * mm, "mid": v(38.1, 0.02) * mm, "end": v(38.36, 0.1) * mm});
            skArc(sketch, "E15.18.13", {"start": v(41.16, 3.2) * mm, "mid": v(41.1, 3.4) * mm, "end": v(40.95, 3.56) * mm});
            skArc(sketch, "E15.18.14", {"start": v(38.04, 4.9) * mm, "mid": v(37.78, 4.95) * mm, "end": v(37.52, 4.96) * mm});
            skArc(sketch, "E15.18.15", {"start": v(41.06, 1.82) * mm, "mid": v(41.18, 1.99) * mm, "end": v(41.23, 2.2) * mm});
            skArc(sketch, "E15.19.0", {"start": v(35.16, 9.3) * mm, "mid": v(34.29, 8.58) * mm, "end": v(34.12, 7.46) * mm});
            skArc(sketch, "E15.19.1", {"start": v(31.61, 14.85) * mm, "mid": v(32.43, 14.07) * mm, "end": v(33.56, 14.02) * mm});
            skLineSegment(sketch, "E15.19.2", {"start": v(36.56, 9.78) * mm, "end": v(35.16, 9.3) * mm});
            skLineSegment(sketch, "E15.19.3", {"start": v(34.96, 14.5) * mm, "end": v(33.56, 14.02) * mm});
            skPoint(sketch, "E15.19.4", {"position": v(39.31, 12.58) * mm});
            skPoint(sketch, "E15.19.5", {"position": v(38.84, 13.96) * mm});
            skArc(sketch, "E15.19.6", {"start": v(35.48, 14.58) * mm, "mid": v(37.08, 14.44) * mm, "end": v(38.63, 14.03) * mm});
            skPoint(sketch, "E15.19.7", {"position": v(35.2, 14.58) * mm});
            skPoint(sketch, "E15.19.8", {"position": v(36.8, 9.86) * mm});
            skArc(sketch, "E15.19.9", {"start": v(37.02, 10.03) * mm, "mid": v(38.2, 11.11) * mm, "end": v(39.2, 12.38) * mm});
            skLineSegment(sketch, "E15.19.10", {"start": v(39.26, 12.79) * mm, "end": v(39.12, 13.28) * mm});
            skLineSegment(sketch, "E15.19.11", {"start": v(38.93, 13.75) * mm, "end": v(39.12, 13.28) * mm});
            skArc(sketch, "E15.19.12", {"start": v(36.56, 9.78) * mm, "mid": v(36.8, 9.88) * mm, "end": v(37.02, 10.03) * mm});
            skArc(sketch, "E15.19.13", {"start": v(38.93, 13.75) * mm, "mid": v(38.8, 13.92) * mm, "end": v(38.63, 14.03) * mm});
            skArc(sketch, "E15.19.14", {"start": v(35.48, 14.58) * mm, "mid": v(35.22, 14.56) * mm, "end": v(34.96, 14.5) * mm});
            skArc(sketch, "E15.19.15", {"start": v(39.2, 12.38) * mm, "mid": v(39.27, 12.58) * mm, "end": v(39.26, 12.79) * mm});
            skArc(sketch, "E15.20.0", {"start": v(31.55, 18.09) * mm, "mid": v(30.9, 17.16) * mm, "end": v(31.03, 16.04) * mm});
            skArc(sketch, "E15.20.1", {"start": v(26.69, 22.53) * mm, "mid": v(27.68, 21.98) * mm, "end": v(28.78, 22.23) * mm});
            skLineSegment(sketch, "E15.20.2", {"start": v(32.79, 18.9) * mm, "end": v(31.55, 18.09) * mm});
            skLineSegment(sketch, "E15.20.3", {"start": v(30.02, 23.05) * mm, "end": v(28.78, 22.23) * mm});
            skPoint(sketch, "E15.20.4", {"position": v(34.72, 22.32) * mm});
            skPoint(sketch, "E15.20.5", {"position": v(33.9, 23.53) * mm});
            skArc(sketch, "E15.20.6", {"start": v(30.5, 23.27) * mm, "mid": v(32.08, 23.55) * mm, "end": v(33.68, 23.55) * mm});
            skPoint(sketch, "E15.20.7", {"position": v(30.23, 23.2) * mm});
            skPoint(sketch, "E15.20.8", {"position": v(33, 19.05) * mm});
            skArc(sketch, "E15.20.9", {"start": v(33.17, 19.27) * mm, "mid": v(34.03, 20.62) * mm, "end": v(34.65, 22.1) * mm});
            skLineSegment(sketch, "E15.20.10", {"start": v(34.6, 22.51) * mm, "end": v(34.35, 22.95) * mm});
            skLineSegment(sketch, "E15.20.11", {"start": v(34.04, 23.36) * mm, "end": v(34.35, 22.95) * mm});
            skArc(sketch, "E15.20.12", {"start": v(32.79, 18.9) * mm, "mid": v(33, 19.07) * mm, "end": v(33.17, 19.27) * mm});
            skArc(sketch, "E15.20.13", {"start": v(34.04, 23.36) * mm, "mid": v(33.88, 23.5) * mm, "end": v(33.68, 23.55) * mm});
            skArc(sketch, "E15.20.14", {"start": v(30.5, 23.27) * mm, "mid": v(30.25, 23.18) * mm, "end": v(30.02, 23.05) * mm});
            skArc(sketch, "E15.20.15", {"start": v(34.65, 22.1) * mm, "mid": v(34.67, 22.31) * mm, "end": v(34.6, 22.51) * mm});
            skArc(sketch, "E15.21.0", {"start": v(25.8, 25.64) * mm, "mid": v(25.4, 24.57) * mm, "end": v(25.82, 23.52) * mm});
            skArc(sketch, "E15.21.1", {"start": v(19.95, 28.67) * mm, "mid": v(21.05, 28.4) * mm, "end": v(22.05, 28.92) * mm});
            skLineSegment(sketch, "E15.21.2", {"start": v(26.77, 26.75) * mm, "end": v(25.8, 25.64) * mm});
            skLineSegment(sketch, "E15.21.3", {"start": v(23.03, 30.04) * mm, "end": v(22.05, 28.92) * mm});
            skPoint(sketch, "E15.21.4", {"position": v(27.76, 30.55) * mm});
            skPoint(sketch, "E15.21.5", {"position": v(26.66, 31.5) * mm});
            skArc(sketch, "E15.21.6", {"start": v(23.43, 30.37) * mm, "mid": v(24.89, 31.05) * mm, "end": v(26.44, 31.47) * mm});
            skPoint(sketch, "E15.21.7", {"position": v(23.2, 30.23) * mm});
            skPoint(sketch, "E15.21.8", {"position": v(26.94, 26.94) * mm});
            skArc(sketch, "E15.21.9", {"start": v(27.05, 27.2) * mm, "mid": v(27.53, 28.73) * mm, "end": v(27.75, 30.32) * mm});
            skLineSegment(sketch, "E15.21.10", {"start": v(27.6, 30.7) * mm, "end": v(27.24, 31.06) * mm});
            skLineSegment(sketch, "E15.21.11", {"start": v(26.84, 31.37) * mm, "end": v(27.24, 31.06) * mm});
            skArc(sketch, "E15.21.12", {"start": v(26.77, 26.75) * mm, "mid": v(26.93, 26.96) * mm, "end": v(27.05, 27.2) * mm});
            skArc(sketch, "E15.21.13", {"start": v(26.84, 31.37) * mm, "mid": v(26.65, 31.46) * mm, "end": v(26.44, 31.47) * mm});
            skArc(sketch, "E15.21.14", {"start": v(23.43, 30.37) * mm, "mid": v(23.22, 30.22) * mm, "end": v(23.03, 30.04) * mm});
            skArc(sketch, "E15.21.15", {"start": v(27.75, 30.32) * mm, "mid": v(27.72, 30.53) * mm, "end": v(27.6, 30.7) * mm});
            skArc(sketch, "E15.22.0", {"start": v(18.28, 31.44) * mm, "mid": v(18.18, 30.31) * mm, "end": v(18.85, 29.4) * mm});
            skArc(sketch, "E15.22.1", {"start": v(11.85, 32.85) * mm, "mid": v(12.98, 32.87) * mm, "end": v(13.81, 33.64) * mm});
            skLineSegment(sketch, "E15.22.2", {"start": v(18.94, 32.77) * mm, "end": v(18.28, 31.44) * mm});
            skLineSegment(sketch, "E15.22.3", {"start": v(14.47, 34.97) * mm, "end": v(13.81, 33.64) * mm});
            skPoint(sketch, "E15.22.4", {"position": v(18.9, 36.7) * mm});
            skPoint(sketch, "E15.22.5", {"position": v(17.6, 37.33) * mm});
            skArc(sketch, "E15.22.6", {"start": v(14.77, 35.4) * mm, "mid": v(16, 36.43) * mm, "end": v(17.4, 37.24) * mm});
            skPoint(sketch, "E15.22.7", {"position": v(14.58, 35.2) * mm});
            skPoint(sketch, "E15.22.8", {"position": v(19.05, 33) * mm});
            skArc(sketch, "E15.22.9", {"start": v(19.09, 33.27) * mm, "mid": v(19.16, 34.87) * mm, "end": v(18.96, 36.47) * mm});
            skLineSegment(sketch, "E15.22.10", {"start": v(18.71, 36.8) * mm, "end": v(18.27, 37.06) * mm});
            skLineSegment(sketch, "E15.22.11", {"start": v(17.8, 37.25) * mm, "end": v(18.27, 37.06) * mm});
            skArc(sketch, "E15.22.12", {"start": v(18.94, 32.77) * mm, "mid": v(19.03, 33.01) * mm, "end": v(19.09, 33.27) * mm});
            skArc(sketch, "E15.22.13", {"start": v(17.8, 37.25) * mm, "mid": v(17.6, 37.29) * mm, "end": v(17.4, 37.24) * mm});
            skArc(sketch, "E15.22.14", {"start": v(14.77, 35.4) * mm, "mid": v(14.6, 35.2) * mm, "end": v(14.47, 34.97) * mm});
            skArc(sketch, "E15.22.15", {"start": v(18.96, 36.47) * mm, "mid": v(18.87, 36.66) * mm, "end": v(18.71, 36.8) * mm});
            skArc(sketch, "E15.23.0", {"start": v(9.52, 35.1) * mm, "mid": v(9.71, 33.98) * mm, "end": v(10.6, 33.28) * mm});
            skArc(sketch, "E15.23.1", {"start": v(2.94, 34.8) * mm, "mid": v(4.03, 35.11) * mm, "end": v(4.63, 36.07) * mm});
            skLineSegment(sketch, "E15.23.2", {"start": v(9.81, 36.55) * mm, "end": v(9.52, 35.1) * mm});
            skLineSegment(sketch, "E15.23.3", {"start": v(4.92, 37.53) * mm, "end": v(4.63, 36.07) * mm});
            skPoint(sketch, "E15.23.4", {"position": v(8.77, 40.33) * mm});
            skPoint(sketch, "E15.23.5", {"position": v(7.34, 40.62) * mm});
            skArc(sketch, "E15.23.6", {"start": v(5.1, 38.02) * mm, "mid": v(6.03, 39.33) * mm, "end": v(7.16, 40.47) * mm});
            skPoint(sketch, "E15.23.7", {"position": v(4.97, 37.77) * mm});
            skPoint(sketch, "E15.23.8", {"position": v(9.86, 36.8) * mm});
            skArc(sketch, "E15.23.9", {"start": v(9.83, 37.08) * mm, "mid": v(9.48, 38.64) * mm, "end": v(8.87, 40.13) * mm});
            skLineSegment(sketch, "E15.23.10", {"start": v(8.55, 40.4) * mm, "end": v(8.06, 40.52) * mm});
            skLineSegment(sketch, "E15.23.11", {"start": v(7.56, 40.59) * mm, "end": v(8.06, 40.52) * mm});
            skArc(sketch, "E15.23.12", {"start": v(9.81, 36.55) * mm, "mid": v(9.84, 36.81) * mm, "end": v(9.83, 37.08) * mm});
            skArc(sketch, "E15.23.13", {"start": v(7.56, 40.59) * mm, "mid": v(7.35, 40.57) * mm, "end": v(7.16, 40.47) * mm});
            skArc(sketch, "E15.23.14", {"start": v(5.1, 38.02) * mm, "mid": v(5, 37.78) * mm, "end": v(4.92, 37.53) * mm});
            skArc(sketch, "E15.23.15", {"start": v(8.87, 40.13) * mm, "mid": v(8.74, 40.3) * mm, "end": v(8.55, 40.4) * mm});
            skArc(sketch, "E16.trimOffspring", {"start": v(-14.85, 31.61) * mm, "mid": v(-15.45, 31.32) * mm, "end": v(-16.04, 31.03) * mm});
            skArc(sketch, "E17.trimOffspring", {"start": v(-22.53, 26.69) * mm, "mid": v(-23.03, 26.26) * mm, "end": v(-23.52, 25.82) * mm});
            skArc(sketch, "E18.trimOffspring", {"start": v(-28.67, 19.95) * mm, "mid": v(-29.04, 19.4) * mm, "end": v(-29.4, 18.85) * mm});
            skArc(sketch, "E19.trimOffspring", {"start": v(-32.85, 11.85) * mm, "mid": v(-33.07, 11.23) * mm, "end": v(-33.28, 10.6) * mm});
            skArc(sketch, "E20.trimOffspring", {"start": v(-34.8, 2.94) * mm, "mid": v(-34.85, 2.28) * mm, "end": v(-34.89, 1.62) * mm});
            skArc(sketch, "E21.trimOffspring", {"start": v(-34.38, -6.16) * mm, "mid": v(-34.25, -6.81) * mm, "end": v(-34.12, -7.46) * mm});
            skArc(sketch, "E22.trimOffspring", {"start": v(-31.61, -14.85) * mm, "mid": v(-31.32, -15.45) * mm, "end": v(-31.03, -16.04) * mm});
            skArc(sketch, "E23.trimOffspring", {"start": v(-26.69, -22.53) * mm, "mid": v(-26.26, -23.03) * mm, "end": v(-25.82, -23.52) * mm});
            skArc(sketch, "E24.trimOffspring", {"start": v(-19.95, -28.67) * mm, "mid": v(-19.4, -29.04) * mm, "end": v(-18.85, -29.4) * mm});
            skArc(sketch, "E25.trimOffspring", {"start": v(-11.85, -32.85) * mm, "mid": v(-11.23, -33.07) * mm, "end": v(-10.6, -33.28) * mm});
            skArc(sketch, "E26.trimOffspring", {"start": v(-2.94, -34.8) * mm, "mid": v(-2.28, -34.85) * mm, "end": v(-1.62, -34.89) * mm});
            skArc(sketch, "E27.trimOffspring", {"start": v(6.16, -34.38) * mm, "mid": v(6.81, -34.25) * mm, "end": v(7.46, -34.12) * mm});
            skArc(sketch, "E28.trimOffspring", {"start": v(14.85, -31.61) * mm, "mid": v(15.45, -31.32) * mm, "end": v(16.04, -31.03) * mm});
            skArc(sketch, "E29.trimOffspring", {"start": v(22.53, -26.69) * mm, "mid": v(23.03, -26.26) * mm, "end": v(23.52, -25.82) * mm});
            skArc(sketch, "E30.trimOffspring", {"start": v(28.67, -19.95) * mm, "mid": v(29.04, -19.4) * mm, "end": v(29.4, -18.85) * mm});
            skArc(sketch, "E31.trimOffspring", {"start": v(32.85, -11.85) * mm, "mid": v(33.07, -11.23) * mm, "end": v(33.28, -10.6) * mm});
            skArc(sketch, "E32.trimOffspring", {"start": v(34.8, -2.94) * mm, "mid": v(34.85, -2.28) * mm, "end": v(34.89, -1.62) * mm});
            skArc(sketch, "E33.trimOffspring", {"start": v(34.38, 6.16) * mm, "mid": v(34.25, 6.81) * mm, "end": v(34.12, 7.46) * mm});
            skArc(sketch, "E34.trimOffspring", {"start": v(31.61, 14.85) * mm, "mid": v(31.32, 15.45) * mm, "end": v(31.03, 16.04) * mm});
            skArc(sketch, "E35.trimOffspring", {"start": v(26.69, 22.53) * mm, "mid": v(26.26, 23.03) * mm, "end": v(25.82, 23.52) * mm});
            skArc(sketch, "E36.trimOffspring", {"start": v(19.95, 28.67) * mm, "mid": v(19.4, 29.04) * mm, "end": v(18.85, 29.4) * mm});
            skArc(sketch, "E37.trimOffspring", {"start": v(11.85, 32.85) * mm, "mid": v(11.23, 33.07) * mm, "end": v(10.6, 33.28) * mm});
            skArc(sketch, "E38.trimOffspring", {"start": v(2.94, 34.8) * mm, "mid": v(2.28, 34.85) * mm, "end": v(1.62, 34.89) * mm});
            skSolve(sketch);
        }
        {
            var Q0;
            Q0=qCreatedBy(makeId("Front.planeOp"),FACE);
            cPlane(context, id + "F1", {"entities" : qUnion([Q0]), "cplaneType" : CPlaneType.OFFSET, "offset" : 50.8 * mm, "width" : 152.4 * mm, "height" : 152.4 * mm});
        }
        {
            var Q0;
            Q0=qCreatedBy(id+"F1.planeOp",FACE);
            var sketch = newSketch(context, id + "F2", { "sketchPlane" : qUnion([Q0])});
            skArc(sketch, "E39", {"start": v(-6.14, 34.05) * mm, "mid": v(-6.8, 33.93) * mm, "end": v(-7.44, 33.8) * mm});
            skArc(sketch, "E40.trimOffspring", {"start": v(-0.08, 38.03) * mm, "mid": v(-0.82, 39.45) * mm, "end": v(-1.8, 40.73) * mm});
            skLineSegment(sketch, "E41", {"start": v(0.04, 37.52) * mm, "end": v(0.13, 36.04) * mm});
            skLineSegment(sketch, "E42", {"start": v(-2.17, 40.9) * mm, "end": v(-2.68, 40.9) * mm});
            skLineSegment(sketch, "E43.MirrorCS", {"start": v(-3.18, 40.83) * mm, "end": v(-2.68, 40.9) * mm});
            skArc(sketch, "E44.MirrorCS", {"start": v(-4.88, 37.71) * mm, "mid": v(-4.33, 39.22) * mm, "end": v(-3.54, 40.62) * mm});
            skLineSegment(sketch, "E45.MirrorCS", {"start": v(-4.94, 37.2) * mm, "end": v(-4.84, 35.72) * mm});
            skPoint(sketch, "E46.orphan", {"position": v(0.35, 32.78) * mm});
            skPoint(sketch, "E47.orphan", {"position": v(-4.62, 32.46) * mm});
            skPoint(sketch, "E48.visualSharp", {"position": v(0.23, 34.6) * mm});
            skArc(sketch, "E48.filletArc", {"start": v(0.13, 36.04) * mm, "mid": v(0.6, 35.01) * mm, "end": v(1.65, 34.56) * mm});
            skPoint(sketch, "E49.visualSharp", {"position": v(-4.74, 34.27) * mm});
            skArc(sketch, "E49.filletArc", {"start": v(-6.14, 34.05) * mm, "mid": v(-5.17, 34.63) * mm, "end": v(-4.84, 35.72) * mm});
            skPoint(sketch, "E50.visualSharp", {"position": v(-3.4, 40.8) * mm});
            skArc(sketch, "E50.filletArc", {"start": v(-3.18, 40.83) * mm, "mid": v(-3.38, 40.76) * mm, "end": v(-3.54, 40.62) * mm});
            skPoint(sketch, "E51.visualSharp", {"position": v(-1.95, 40.9) * mm});
            skArc(sketch, "E51.filletArc", {"start": v(-1.8, 40.73) * mm, "mid": v(-1.97, 40.86) * mm, "end": v(-2.17, 40.9) * mm});
            skPoint(sketch, "E52.visualSharp", {"position": v(-4.95, 37.45) * mm});
            skArc(sketch, "E52.filletArc", {"start": v(-4.88, 37.71) * mm, "mid": v(-4.93, 37.46) * mm, "end": v(-4.94, 37.2) * mm});
            skPoint(sketch, "E53.visualSharp", {"position": v(0.02, 37.77) * mm});
            skArc(sketch, "E53.filletArc", {"start": v(0.04, 37.52) * mm, "mid": v(0, 37.78) * mm, "end": v(-0.08, 38.03) * mm});
            skArc(sketch, "E54.1.0", {"start": v(-9.28, 34.83) * mm, "mid": v(-8.56, 33.96) * mm, "end": v(-7.44, 33.8) * mm});
            skArc(sketch, "E54.1.1", {"start": v(-14.83, 31.28) * mm, "mid": v(-14.04, 32.1) * mm, "end": v(-14, 33.23) * mm});
            skLineSegment(sketch, "E54.1.2", {"start": v(-9.76, 36.23) * mm, "end": v(-9.28, 34.83) * mm});
            skLineSegment(sketch, "E54.1.3", {"start": v(-14.48, 34.63) * mm, "end": v(-14, 33.23) * mm});
            skPoint(sketch, "E54.1.4", {"position": v(-12.55, 38.98) * mm});
            skPoint(sketch, "E54.1.5", {"position": v(-13.93, 38.52) * mm});
            skArc(sketch, "E54.1.6", {"start": v(-14.56, 35.15) * mm, "mid": v(-14.42, 36.75) * mm, "end": v(-14.01, 38.3) * mm});
            skPoint(sketch, "E54.1.7", {"position": v(-14.56, 34.87) * mm});
            skPoint(sketch, "E54.1.8", {"position": v(-9.84, 36.47) * mm});
            skArc(sketch, "E54.1.9", {"start": v(-10, 36.7) * mm, "mid": v(-11.1, 37.88) * mm, "end": v(-12.36, 38.86) * mm});
            skLineSegment(sketch, "E54.1.10", {"start": v(-12.77, 38.93) * mm, "end": v(-13.26, 38.8) * mm});
            skLineSegment(sketch, "E54.1.11", {"start": v(-13.73, 38.6) * mm, "end": v(-13.26, 38.8) * mm});
            skArc(sketch, "E54.1.12", {"start": v(-9.76, 36.23) * mm, "mid": v(-9.86, 36.48) * mm, "end": v(-10, 36.7) * mm});
            skArc(sketch, "E54.1.13", {"start": v(-13.73, 38.6) * mm, "mid": v(-13.9, 38.48) * mm, "end": v(-14.01, 38.3) * mm});
            skArc(sketch, "E54.1.14", {"start": v(-14.56, 35.15) * mm, "mid": v(-14.54, 34.89) * mm, "end": v(-14.48, 34.63) * mm});
            skArc(sketch, "E54.1.15", {"start": v(-12.36, 38.86) * mm, "mid": v(-12.56, 38.94) * mm, "end": v(-12.77, 38.93) * mm});
            skArc(sketch, "E54.2.0", {"start": v(-18.06, 31.23) * mm, "mid": v(-17.14, 30.57) * mm, "end": v(-16.02, 30.7) * mm});
            skArc(sketch, "E54.2.1", {"start": v(-22.5, 26.36) * mm, "mid": v(-21.96, 27.35) * mm, "end": v(-22.2, 28.46) * mm});
            skLineSegment(sketch, "E54.2.2", {"start": v(-18.89, 32.46) * mm, "end": v(-18.06, 31.23) * mm});
            skLineSegment(sketch, "E54.2.3", {"start": v(-23.03, 29.69) * mm, "end": v(-22.2, 28.46) * mm});
            skPoint(sketch, "E54.2.4", {"position": v(-22.3, 34.4) * mm});
            skPoint(sketch, "E54.2.5", {"position": v(-23.51, 33.58) * mm});
            skArc(sketch, "E54.2.6", {"start": v(-23.25, 30.17) * mm, "mid": v(-23.52, 31.75) * mm, "end": v(-23.53, 33.35) * mm});
            skPoint(sketch, "E54.2.7", {"position": v(-23.17, 29.9) * mm});
            skPoint(sketch, "E54.2.8", {"position": v(-19.03, 32.67) * mm});
            skArc(sketch, "E54.2.9", {"start": v(-19.25, 32.84) * mm, "mid": v(-20.6, 33.7) * mm, "end": v(-22.08, 34.32) * mm});
            skLineSegment(sketch, "E54.2.10", {"start": v(-22.5, 34.28) * mm, "end": v(-22.93, 34.03) * mm});
            skLineSegment(sketch, "E54.2.11", {"start": v(-23.34, 33.72) * mm, "end": v(-22.93, 34.03) * mm});
            skArc(sketch, "E54.2.12", {"start": v(-18.89, 32.46) * mm, "mid": v(-19.05, 32.66) * mm, "end": v(-19.25, 32.84) * mm});
            skArc(sketch, "E54.2.13", {"start": v(-23.34, 33.72) * mm, "mid": v(-23.47, 33.56) * mm, "end": v(-23.53, 33.35) * mm});
            skArc(sketch, "E54.2.14", {"start": v(-23.25, 30.17) * mm, "mid": v(-23.16, 29.92) * mm, "end": v(-23.03, 29.69) * mm});
            skArc(sketch, "E54.2.15", {"start": v(-22.08, 34.32) * mm, "mid": v(-22.3, 34.34) * mm, "end": v(-22.5, 34.28) * mm});
            skArc(sketch, "E54.3.0", {"start": v(-25.62, 25.47) * mm, "mid": v(-24.55, 25.08) * mm, "end": v(-23.5, 25.49) * mm});
            skArc(sketch, "E54.3.1", {"start": v(-28.64, 19.62) * mm, "mid": v(-28.37, 20.72) * mm, "end": v(-28.9, 21.72) * mm});
            skLineSegment(sketch, "E54.3.2", {"start": v(-26.73, 26.45) * mm, "end": v(-25.62, 25.47) * mm});
            skLineSegment(sketch, "E54.3.3", {"start": v(-30.02, 22.7) * mm, "end": v(-28.9, 21.72) * mm});
            skPoint(sketch, "E54.3.4", {"position": v(-30.53, 27.43) * mm});
            skPoint(sketch, "E54.3.5", {"position": v(-31.49, 26.33) * mm});
            skArc(sketch, "E54.3.6", {"start": v(-30.35, 23.1) * mm, "mid": v(-31.02, 24.56) * mm, "end": v(-31.45, 26.1) * mm});
            skPoint(sketch, "E54.3.7", {"position": v(-30.2, 22.87) * mm});
            skPoint(sketch, "E54.3.8", {"position": v(-26.92, 26.61) * mm});
            skArc(sketch, "E54.3.9", {"start": v(-27.17, 26.72) * mm, "mid": v(-28.7, 27.2) * mm, "end": v(-30.3, 27.42) * mm});
            skLineSegment(sketch, "E54.3.10", {"start": v(-30.68, 27.27) * mm, "end": v(-31.04, 26.91) * mm});
            skLineSegment(sketch, "E54.3.11", {"start": v(-31.35, 26.51) * mm, "end": v(-31.04, 26.91) * mm});
            skArc(sketch, "E54.3.12", {"start": v(-26.73, 26.45) * mm, "mid": v(-26.94, 26.6) * mm, "end": v(-27.17, 26.72) * mm});
            skArc(sketch, "E54.3.13", {"start": v(-31.35, 26.51) * mm, "mid": v(-31.44, 26.32) * mm, "end": v(-31.45, 26.1) * mm});
            skArc(sketch, "E54.3.14", {"start": v(-30.35, 23.1) * mm, "mid": v(-30.2, 22.89) * mm, "end": v(-30.02, 22.7) * mm});
            skArc(sketch, "E54.3.15", {"start": v(-30.3, 27.42) * mm, "mid": v(-30.5, 27.39) * mm, "end": v(-30.68, 27.27) * mm});
            skArc(sketch, "E54.4.0", {"start": v(-31.42, 17.95) * mm, "mid": v(-30.3, 17.85) * mm, "end": v(-29.38, 18.52) * mm});
            skArc(sketch, "E54.4.1", {"start": v(-32.83, 11.52) * mm, "mid": v(-32.85, 12.65) * mm, "end": v(-33.62, 13.49) * mm});
            skLineSegment(sketch, "E54.4.2", {"start": v(-32.75, 18.61) * mm, "end": v(-31.42, 17.95) * mm});
            skLineSegment(sketch, "E54.4.3", {"start": v(-34.95, 14.14) * mm, "end": v(-33.62, 13.49) * mm});
            skPoint(sketch, "E54.4.4", {"position": v(-36.67, 18.58) * mm});
            skPoint(sketch, "E54.4.5", {"position": v(-37.31, 17.27) * mm});
            skArc(sketch, "E54.4.6", {"start": v(-35.38, 14.45) * mm, "mid": v(-36.4, 15.68) * mm, "end": v(-37.22, 17.06) * mm});
            skPoint(sketch, "E54.4.7", {"position": v(-35.18, 14.25) * mm});
            skPoint(sketch, "E54.4.8", {"position": v(-32.97, 18.72) * mm});
            skArc(sketch, "E54.4.9", {"start": v(-33.25, 18.76) * mm, "mid": v(-34.85, 18.83) * mm, "end": v(-36.45, 18.63) * mm});
            skLineSegment(sketch, "E54.4.10", {"start": v(-36.78, 18.39) * mm, "end": v(-37.03, 17.95) * mm});
            skLineSegment(sketch, "E54.4.11", {"start": v(-37.23, 17.48) * mm, "end": v(-37.03, 17.95) * mm});
            skArc(sketch, "E54.4.12", {"start": v(-32.75, 18.61) * mm, "mid": v(-33, 18.7) * mm, "end": v(-33.25, 18.76) * mm});
            skArc(sketch, "E54.4.13", {"start": v(-37.23, 17.48) * mm, "mid": v(-37.27, 17.27) * mm, "end": v(-37.22, 17.06) * mm});
            skArc(sketch, "E54.4.14", {"start": v(-35.38, 14.45) * mm, "mid": v(-35.18, 14.28) * mm, "end": v(-34.95, 14.14) * mm});
            skArc(sketch, "E54.4.15", {"start": v(-36.45, 18.63) * mm, "mid": v(-36.64, 18.54) * mm, "end": v(-36.78, 18.39) * mm});
            skArc(sketch, "E54.5.0", {"start": v(-35.08, 9.2) * mm, "mid": v(-33.96, 9.38) * mm, "end": v(-33.26, 10.27) * mm});
            skArc(sketch, "E54.5.1", {"start": v(-34.78, 2.62) * mm, "mid": v(-35.1, 3.7) * mm, "end": v(-36.05, 4.3) * mm});
            skLineSegment(sketch, "E54.5.2", {"start": v(-36.53, 9.48) * mm, "end": v(-35.08, 9.2) * mm});
            skLineSegment(sketch, "E54.5.3", {"start": v(-37.5, 4.6) * mm, "end": v(-36.05, 4.3) * mm});
            skPoint(sketch, "E54.5.4", {"position": v(-40.31, 8.44) * mm});
            skPoint(sketch, "E54.5.5", {"position": v(-40.6, 7) * mm});
            skArc(sketch, "E54.5.6", {"start": v(-38, 4.78) * mm, "mid": v(-39.3, 5.7) * mm, "end": v(-40.45, 6.83) * mm});
            skPoint(sketch, "E54.5.7", {"position": v(-37.75, 4.65) * mm});
            skPoint(sketch, "E54.5.8", {"position": v(-36.78, 9.53) * mm});
            skArc(sketch, "E54.5.9", {"start": v(-37.05, 9.5) * mm, "mid": v(-38.62, 9.15) * mm, "end": v(-40.1, 8.54) * mm});
            skLineSegment(sketch, "E54.5.10", {"start": v(-40.37, 8.22) * mm, "end": v(-40.5, 7.73) * mm});
            skLineSegment(sketch, "E54.5.11", {"start": v(-40.57, 7.23) * mm, "end": v(-40.5, 7.73) * mm});
            skArc(sketch, "E54.5.12", {"start": v(-36.53, 9.48) * mm, "mid": v(-36.8, 9.51) * mm, "end": v(-37.05, 9.5) * mm});
            skArc(sketch, "E54.5.13", {"start": v(-40.57, 7.23) * mm, "mid": v(-40.55, 7.02) * mm, "end": v(-40.45, 6.83) * mm});
            skArc(sketch, "E54.5.14", {"start": v(-38, 4.78) * mm, "mid": v(-37.76, 4.67) * mm, "end": v(-37.5, 4.6) * mm});
            skArc(sketch, "E54.5.15", {"start": v(-40.1, 8.54) * mm, "mid": v(-40.27, 8.41) * mm, "end": v(-40.37, 8.22) * mm});
            skArc(sketch, "E54.6.0", {"start": v(-36.35, -0.21) * mm, "mid": v(-35.32, 0.26) * mm, "end": v(-34.87, 1.3) * mm});
            skArc(sketch, "E54.6.1", {"start": v(-34.36, -6.5) * mm, "mid": v(-34.94, -5.52) * mm, "end": v(-36.02, -5.19) * mm});
            skLineSegment(sketch, "E54.6.2", {"start": v(-37.83, -0.31) * mm, "end": v(-36.35, -0.21) * mm});
            skLineSegment(sketch, "E54.6.3", {"start": v(-37.5, -5.28) * mm, "end": v(-36.02, -5.19) * mm});
            skPoint(sketch, "E54.6.4", {"position": v(-41.2, -2.3) * mm});
            skPoint(sketch, "E54.6.5", {"position": v(-41.11, -3.75) * mm});
            skArc(sketch, "E54.6.6", {"start": v(-38.02, -5.23) * mm, "mid": v(-39.53, -4.68) * mm, "end": v(-40.92, -3.89) * mm});
            skPoint(sketch, "E54.6.7", {"position": v(-37.75, -5.3) * mm});
            skPoint(sketch, "E54.6.8", {"position": v(-38.08, -0.33) * mm});
            skArc(sketch, "E54.6.9", {"start": v(-38.34, -0.43) * mm, "mid": v(-39.76, -1.17) * mm, "end": v(-41.04, -2.14) * mm});
            skLineSegment(sketch, "E54.6.10", {"start": v(-41.2, -2.52) * mm, "end": v(-41.2, -3.03) * mm});
            skLineSegment(sketch, "E54.6.11", {"start": v(-41.14, -3.53) * mm, "end": v(-41.2, -3.03) * mm});
            skArc(sketch, "E54.6.12", {"start": v(-37.83, -0.31) * mm, "mid": v(-38.09, -0.35) * mm, "end": v(-38.34, -0.43) * mm});
            skArc(sketch, "E54.6.13", {"start": v(-41.14, -3.53) * mm, "mid": v(-41.07, -3.73) * mm, "end": v(-40.92, -3.89) * mm});
            skArc(sketch, "E54.6.14", {"start": v(-38.02, -5.23) * mm, "mid": v(-37.76, -5.28) * mm, "end": v(-37.5, -5.28) * mm});
            skArc(sketch, "E54.6.15", {"start": v(-41.04, -2.14) * mm, "mid": v(-41.16, -2.32) * mm, "end": v(-41.2, -2.52) * mm});
            skArc(sketch, "E54.7.0", {"start": v(-35.14, -9.63) * mm, "mid": v(-34.27, -8.9) * mm, "end": v(-34.1, -7.79) * mm});
            skArc(sketch, "E54.7.1", {"start": v(-31.59, -15.18) * mm, "mid": v(-32.4, -14.4) * mm, "end": v(-33.54, -14.35) * mm});
            skLineSegment(sketch, "E54.7.2", {"start": v(-36.54, -10.1) * mm, "end": v(-35.14, -9.63) * mm});
            skLineSegment(sketch, "E54.7.3", {"start": v(-34.94, -14.83) * mm, "end": v(-33.54, -14.35) * mm});
            skPoint(sketch, "E54.7.4", {"position": v(-39.3, -12.9) * mm});
            skPoint(sketch, "E54.7.5", {"position": v(-38.82, -14.28) * mm});
            skArc(sketch, "E54.7.6", {"start": v(-35.45, -14.91) * mm, "mid": v(-37.05, -14.77) * mm, "end": v(-38.6, -14.36) * mm});
            skPoint(sketch, "E54.7.7", {"position": v(-35.18, -14.9) * mm});
            skPoint(sketch, "E54.7.8", {"position": v(-36.78, -10.19) * mm});
            skArc(sketch, "E54.7.9", {"start": v(-37, -10.35) * mm, "mid": v(-38.19, -11.44) * mm, "end": v(-39.17, -12.7) * mm});
            skLineSegment(sketch, "E54.7.10", {"start": v(-39.23, -13.12) * mm, "end": v(-39.1, -13.6) * mm});
            skLineSegment(sketch, "E54.7.11", {"start": v(-38.9, -14.08) * mm, "end": v(-39.1, -13.6) * mm});
            skArc(sketch, "E54.7.12", {"start": v(-36.54, -10.1) * mm, "mid": v(-36.78, -10.21) * mm, "end": v(-37, -10.35) * mm});
            skArc(sketch, "E54.7.13", {"start": v(-38.9, -14.08) * mm, "mid": v(-38.79, -14.25) * mm, "end": v(-38.6, -14.36) * mm});
            skArc(sketch, "E54.7.14", {"start": v(-35.45, -14.91) * mm, "mid": v(-35.2, -14.9) * mm, "end": v(-34.94, -14.83) * mm});
            skArc(sketch, "E54.7.15", {"start": v(-39.17, -12.7) * mm, "mid": v(-39.24, -12.9) * mm, "end": v(-39.23, -13.12) * mm});
            skArc(sketch, "E54.8.0", {"start": v(-31.53, -18.41) * mm, "mid": v(-30.88, -17.5) * mm, "end": v(-31, -16.37) * mm});
            skArc(sketch, "E54.8.1", {"start": v(-26.67, -22.85) * mm, "mid": v(-27.66, -22.3) * mm, "end": v(-28.76, -22.56) * mm});
            skLineSegment(sketch, "E54.8.2", {"start": v(-32.76, -19.24) * mm, "end": v(-31.53, -18.41) * mm});
            skLineSegment(sketch, "E54.8.3", {"start": v(-30, -23.38) * mm, "end": v(-28.76, -22.56) * mm});
            skPoint(sketch, "E54.8.4", {"position": v(-34.7, -22.65) * mm});
            skPoint(sketch, "E54.8.5", {"position": v(-33.89, -23.86) * mm});
            skArc(sketch, "E54.8.6", {"start": v(-30.47, -23.6) * mm, "mid": v(-32.05, -23.87) * mm, "end": v(-33.66, -23.88) * mm});
            skPoint(sketch, "E54.8.7", {"position": v(-30.2, -23.52) * mm});
            skPoint(sketch, "E54.8.8", {"position": v(-32.97, -19.38) * mm});
            skArc(sketch, "E54.8.9", {"start": v(-33.14, -19.6) * mm, "mid": v(-34, -20.95) * mm, "end": v(-34.63, -22.43) * mm});
            skLineSegment(sketch, "E54.8.10", {"start": v(-34.59, -22.84) * mm, "end": v(-34.33, -23.28) * mm});
            skLineSegment(sketch, "E54.8.11", {"start": v(-34.02, -23.69) * mm, "end": v(-34.33, -23.28) * mm});
            skArc(sketch, "E54.8.12", {"start": v(-32.76, -19.24) * mm, "mid": v(-32.97, -19.4) * mm, "end": v(-33.14, -19.6) * mm});
            skArc(sketch, "E54.8.13", {"start": v(-34.02, -23.69) * mm, "mid": v(-33.86, -23.82) * mm, "end": v(-33.66, -23.88) * mm});
            skArc(sketch, "E54.8.14", {"start": v(-30.47, -23.6) * mm, "mid": v(-30.22, -23.5) * mm, "end": v(-30, -23.38) * mm});
            skArc(sketch, "E54.8.15", {"start": v(-34.63, -22.43) * mm, "mid": v(-34.65, -22.64) * mm, "end": v(-34.59, -22.84) * mm});
            skArc(sketch, "E54.9.0", {"start": v(-25.78, -25.96) * mm, "mid": v(-25.38, -24.9) * mm, "end": v(-25.8, -23.85) * mm});
            skArc(sketch, "E54.9.1", {"start": v(-19.93, -29) * mm, "mid": v(-21.03, -28.72) * mm, "end": v(-22.03, -29.25) * mm});
            skLineSegment(sketch, "E54.9.2", {"start": v(-26.75, -27.08) * mm, "end": v(-25.78, -25.96) * mm});
            skLineSegment(sketch, "E54.9.3", {"start": v(-23, -30.36) * mm, "end": v(-22.03, -29.25) * mm});
            skPoint(sketch, "E54.9.4", {"position": v(-27.74, -30.87) * mm});
            skPoint(sketch, "E54.9.5", {"position": v(-26.64, -31.84) * mm});
            skArc(sketch, "E54.9.6", {"start": v(-23.41, -30.7) * mm, "mid": v(-24.87, -31.37) * mm, "end": v(-26.42, -31.8) * mm});
            skPoint(sketch, "E54.9.7", {"position": v(-23.17, -30.55) * mm});
            skPoint(sketch, "E54.9.8", {"position": v(-26.92, -27.27) * mm});
            skArc(sketch, "E54.9.9", {"start": v(-27.03, -27.52) * mm, "mid": v(-27.5, -29.06) * mm, "end": v(-27.73, -30.65) * mm});
            skLineSegment(sketch, "E54.9.10", {"start": v(-27.58, -31.03) * mm, "end": v(-27.22, -31.4) * mm});
            skLineSegment(sketch, "E54.9.11", {"start": v(-26.82, -31.7) * mm, "end": v(-27.22, -31.4) * mm});
            skArc(sketch, "E54.9.12", {"start": v(-26.75, -27.08) * mm, "mid": v(-26.9, -27.29) * mm, "end": v(-27.03, -27.52) * mm});
            skArc(sketch, "E54.9.13", {"start": v(-26.82, -31.7) * mm, "mid": v(-26.63, -31.8) * mm, "end": v(-26.42, -31.8) * mm});
            skArc(sketch, "E54.9.14", {"start": v(-23.41, -30.7) * mm, "mid": v(-23.2, -30.55) * mm, "end": v(-23, -30.36) * mm});
            skArc(sketch, "E54.9.15", {"start": v(-27.73, -30.65) * mm, "mid": v(-27.7, -30.85) * mm, "end": v(-27.58, -31.03) * mm});
            skArc(sketch, "E54.10.0", {"start": v(-18.26, -31.77) * mm, "mid": v(-18.16, -30.64) * mm, "end": v(-18.83, -29.73) * mm});
            skArc(sketch, "E54.10.1", {"start": v(-11.83, -33.18) * mm, "mid": v(-12.96, -33.2) * mm, "end": v(-13.8, -33.97) * mm});
            skLineSegment(sketch, "E54.10.2", {"start": v(-18.92, -33.1) * mm, "end": v(-18.26, -31.77) * mm});
            skLineSegment(sketch, "E54.10.3", {"start": v(-14.45, -35.3) * mm, "end": v(-13.8, -33.97) * mm});
            skPoint(sketch, "E54.10.4", {"position": v(-18.88, -37.02) * mm});
            skPoint(sketch, "E54.10.5", {"position": v(-17.58, -37.66) * mm});
            skArc(sketch, "E54.10.6", {"start": v(-14.75, -35.73) * mm, "mid": v(-15.98, -36.76) * mm, "end": v(-17.37, -37.57) * mm});
            skPoint(sketch, "E54.10.7", {"position": v(-14.56, -35.53) * mm});
            skPoint(sketch, "E54.10.8", {"position": v(-19.03, -33.32) * mm});
            skArc(sketch, "E54.10.9", {"start": v(-19.07, -33.6) * mm, "mid": v(-19.14, -35.2) * mm, "end": v(-18.94, -36.8) * mm});
            skLineSegment(sketch, "E54.10.10", {"start": v(-18.7, -37.13) * mm, "end": v(-18.25, -37.38) * mm});
            skLineSegment(sketch, "E54.10.11", {"start": v(-17.78, -37.58) * mm, "end": v(-18.25, -37.38) * mm});
            skArc(sketch, "E54.10.12", {"start": v(-18.92, -33.1) * mm, "mid": v(-19.01, -33.34) * mm, "end": v(-19.07, -33.6) * mm});
            skArc(sketch, "E54.10.13", {"start": v(-17.78, -37.58) * mm, "mid": v(-17.58, -37.62) * mm, "end": v(-17.37, -37.57) * mm});
            skArc(sketch, "E54.10.14", {"start": v(-14.75, -35.73) * mm, "mid": v(-14.58, -35.53) * mm, "end": v(-14.45, -35.3) * mm});
            skArc(sketch, "E54.10.15", {"start": v(-18.94, -36.8) * mm, "mid": v(-18.85, -36.99) * mm, "end": v(-18.7, -37.13) * mm});
            skArc(sketch, "E54.11.0", {"start": v(-9.5, -35.43) * mm, "mid": v(-9.7, -34.31) * mm, "end": v(-10.58, -33.6) * mm});
            skArc(sketch, "E54.11.1", {"start": v(-2.92, -35.13) * mm, "mid": v(-4.01, -35.44) * mm, "end": v(-4.61, -36.4) * mm});
            skLineSegment(sketch, "E54.11.2", {"start": v(-9.8, -36.88) * mm, "end": v(-9.5, -35.43) * mm});
            skLineSegment(sketch, "E54.11.3", {"start": v(-4.9, -37.85) * mm, "end": v(-4.61, -36.4) * mm});
            skPoint(sketch, "E54.11.4", {"position": v(-8.74, -40.66) * mm});
            skPoint(sketch, "E54.11.5", {"position": v(-7.31, -40.95) * mm});
            skArc(sketch, "E54.11.6", {"start": v(-5.09, -38.34) * mm, "mid": v(-6, -39.66) * mm, "end": v(-7.14, -40.8) * mm});
            skPoint(sketch, "E54.11.7", {"position": v(-4.95, -38.1) * mm});
            skPoint(sketch, "E54.11.8", {"position": v(-9.84, -37.13) * mm});
            skArc(sketch, "E54.11.9", {"start": v(-9.8, -37.4) * mm, "mid": v(-9.46, -38.97) * mm, "end": v(-8.85, -40.46) * mm});
            skLineSegment(sketch, "E54.11.10", {"start": v(-8.53, -40.72) * mm, "end": v(-8.04, -40.85) * mm});
            skLineSegment(sketch, "E54.11.11", {"start": v(-7.54, -40.92) * mm, "end": v(-8.04, -40.85) * mm});
            skArc(sketch, "E54.11.12", {"start": v(-9.8, -36.88) * mm, "mid": v(-9.82, -37.14) * mm, "end": v(-9.8, -37.4) * mm});
            skArc(sketch, "E54.11.13", {"start": v(-7.54, -40.92) * mm, "mid": v(-7.32, -40.9) * mm, "end": v(-7.14, -40.8) * mm});
            skArc(sketch, "E54.11.14", {"start": v(-5.09, -38.34) * mm, "mid": v(-4.97, -38.1) * mm, "end": v(-4.9, -37.85) * mm});
            skArc(sketch, "E54.11.15", {"start": v(-8.85, -40.46) * mm, "mid": v(-8.72, -40.62) * mm, "end": v(-8.53, -40.72) * mm});
            skArc(sketch, "E54.12.0", {"start": v(-0.1, -36.7) * mm, "mid": v(-0.56, -35.67) * mm, "end": v(-1.6, -35.22) * mm});
            skArc(sketch, "E54.12.1", {"start": v(6.19, -34.7) * mm, "mid": v(5.21, -35.29) * mm, "end": v(4.88, -36.37) * mm});
            skLineSegment(sketch, "E54.12.2", {"start": v(0, -38.18) * mm, "end": v(-0.1, -36.7) * mm});
            skLineSegment(sketch, "E54.12.3", {"start": v(4.98, -37.85) * mm, "end": v(4.88, -36.37) * mm});
            skPoint(sketch, "E54.12.4", {"position": v(2, -41.56) * mm});
            skPoint(sketch, "E54.12.5", {"position": v(3.45, -41.46) * mm});
            skArc(sketch, "E54.12.6", {"start": v(4.93, -38.37) * mm, "mid": v(4.38, -39.88) * mm, "end": v(3.58, -41.27) * mm});
            skPoint(sketch, "E54.12.7", {"position": v(5, -38.1) * mm});
            skPoint(sketch, "E54.12.8", {"position": v(0.02, -38.43) * mm});
            skArc(sketch, "E54.12.9", {"start": v(0.12, -38.68) * mm, "mid": v(0.87, -40.1) * mm, "end": v(1.84, -41.39) * mm});
            skLineSegment(sketch, "E54.12.10", {"start": v(2.22, -41.56) * mm, "end": v(2.72, -41.56) * mm});
            skLineSegment(sketch, "E54.12.11", {"start": v(3.23, -41.49) * mm, "end": v(2.72, -41.56) * mm});
            skArc(sketch, "E54.12.12", {"start": v(0, -38.18) * mm, "mid": v(0.04, -38.44) * mm, "end": v(0.12, -38.68) * mm});
            skArc(sketch, "E54.12.13", {"start": v(3.23, -41.49) * mm, "mid": v(3.43, -41.42) * mm, "end": v(3.58, -41.27) * mm});
            skArc(sketch, "E54.12.14", {"start": v(4.93, -38.37) * mm, "mid": v(4.97, -38.11) * mm, "end": v(4.98, -37.85) * mm});
            skArc(sketch, "E54.12.15", {"start": v(1.84, -41.39) * mm, "mid": v(2, -41.51) * mm, "end": v(2.22, -41.56) * mm});
            skArc(sketch, "E54.13.0", {"start": v(9.32, -35.49) * mm, "mid": v(8.6, -34.62) * mm, "end": v(7.48, -34.45) * mm});
            skArc(sketch, "E54.13.1", {"start": v(14.87, -31.94) * mm, "mid": v(14.09, -32.75) * mm, "end": v(14.04, -33.89) * mm});
            skLineSegment(sketch, "E54.13.2", {"start": v(9.8, -36.9) * mm, "end": v(9.32, -35.49) * mm});
            skLineSegment(sketch, "E54.13.3", {"start": v(14.52, -35.29) * mm, "end": v(14.04, -33.89) * mm});
            skPoint(sketch, "E54.13.4", {"position": v(12.6, -39.64) * mm});
            skPoint(sketch, "E54.13.5", {"position": v(13.98, -39.17) * mm});
            skArc(sketch, "E54.13.6", {"start": v(14.6, -35.8) * mm, "mid": v(14.46, -37.4) * mm, "end": v(14.06, -38.96) * mm});
            skPoint(sketch, "E54.13.7", {"position": v(14.6, -35.53) * mm});
            skPoint(sketch, "E54.13.8", {"position": v(9.88, -37.13) * mm});
            skArc(sketch, "E54.13.9", {"start": v(10.05, -37.35) * mm, "mid": v(11.13, -38.53) * mm, "end": v(12.4, -39.52) * mm});
            skLineSegment(sketch, "E54.13.10", {"start": v(12.81, -39.58) * mm, "end": v(13.3, -39.45) * mm});
            skLineSegment(sketch, "E54.13.11", {"start": v(13.77, -39.26) * mm, "end": v(13.3, -39.45) * mm});
            skArc(sketch, "E54.13.12", {"start": v(9.8, -36.9) * mm, "mid": v(9.9, -37.13) * mm, "end": v(10.05, -37.35) * mm});
            skArc(sketch, "E54.13.13", {"start": v(13.77, -39.26) * mm, "mid": v(13.95, -39.14) * mm, "end": v(14.06, -38.96) * mm});
            skArc(sketch, "E54.13.14", {"start": v(14.6, -35.8) * mm, "mid": v(14.58, -35.54) * mm, "end": v(14.52, -35.29) * mm});
            skArc(sketch, "E54.13.15", {"start": v(12.4, -39.52) * mm, "mid": v(12.6, -39.6) * mm, "end": v(12.81, -39.58) * mm});
            skArc(sketch, "E54.14.0", {"start": v(18.1, -31.88) * mm, "mid": v(17.18, -31.23) * mm, "end": v(16.06, -31.35) * mm});
            skArc(sketch, "E54.14.1", {"start": v(22.55, -27.02) * mm, "mid": v(22, -28) * mm, "end": v(22.25, -29.11) * mm});
            skLineSegment(sketch, "E54.14.2", {"start": v(18.93, -33.11) * mm, "end": v(18.1, -31.88) * mm});
            skLineSegment(sketch, "E54.14.3", {"start": v(23.07, -30.34) * mm, "end": v(22.25, -29.11) * mm});
            skPoint(sketch, "E54.14.4", {"position": v(22.34, -35.05) * mm});
            skPoint(sketch, "E54.14.5", {"position": v(23.56, -34.24) * mm});
            skArc(sketch, "E54.14.6", {"start": v(23.29, -30.82) * mm, "mid": v(23.57, -32.4) * mm, "end": v(23.58, -34) * mm});
            skPoint(sketch, "E54.14.7", {"position": v(23.22, -30.55) * mm});
            skPoint(sketch, "E54.14.8", {"position": v(19.07, -33.32) * mm});
            skArc(sketch, "E54.14.9", {"start": v(19.29, -33.5) * mm, "mid": v(20.64, -34.36) * mm, "end": v(22.12, -34.98) * mm});
            skLineSegment(sketch, "E54.14.10", {"start": v(22.54, -34.94) * mm, "end": v(22.98, -34.68) * mm});
            skLineSegment(sketch, "E54.14.11", {"start": v(23.38, -34.37) * mm, "end": v(22.98, -34.68) * mm});
            skArc(sketch, "E54.14.12", {"start": v(18.93, -33.11) * mm, "mid": v(19.1, -33.32) * mm, "end": v(19.29, -33.5) * mm});
            skArc(sketch, "E54.14.13", {"start": v(23.38, -34.37) * mm, "mid": v(23.52, -34.21) * mm, "end": v(23.58, -34) * mm});
            skArc(sketch, "E54.14.14", {"start": v(23.29, -30.82) * mm, "mid": v(23.2, -30.57) * mm, "end": v(23.07, -30.34) * mm});
            skArc(sketch, "E54.14.15", {"start": v(22.12, -34.98) * mm, "mid": v(22.33, -35) * mm, "end": v(22.54, -34.94) * mm});
            skArc(sketch, "E54.15.0", {"start": v(25.66, -26.13) * mm, "mid": v(24.6, -25.73) * mm, "end": v(23.54, -26.15) * mm});
            skArc(sketch, "E54.15.1", {"start": v(28.69, -20.28) * mm, "mid": v(28.42, -21.38) * mm, "end": v(28.94, -22.38) * mm});
            skLineSegment(sketch, "E54.15.2", {"start": v(26.77, -27.1) * mm, "end": v(25.66, -26.13) * mm});
            skLineSegment(sketch, "E54.15.3", {"start": v(30.06, -23.36) * mm, "end": v(28.94, -22.38) * mm});
            skPoint(sketch, "E54.15.4", {"position": v(30.57, -28.09) * mm});
            skPoint(sketch, "E54.15.5", {"position": v(31.53, -27) * mm});
            skArc(sketch, "E54.15.6", {"start": v(30.39, -23.76) * mm, "mid": v(31.07, -25.22) * mm, "end": v(31.5, -26.77) * mm});
            skPoint(sketch, "E54.15.7", {"position": v(30.25, -23.52) * mm});
            skPoint(sketch, "E54.15.8", {"position": v(26.96, -27.27) * mm});
            skArc(sketch, "E54.15.9", {"start": v(27.22, -27.38) * mm, "mid": v(28.75, -27.86) * mm, "end": v(30.34, -28.08) * mm});
            skLineSegment(sketch, "E54.15.10", {"start": v(30.73, -27.93) * mm, "end": v(31.08, -27.57) * mm});
            skLineSegment(sketch, "E54.15.11", {"start": v(31.4, -27.17) * mm, "end": v(31.08, -27.57) * mm});
            skArc(sketch, "E54.15.12", {"start": v(26.77, -27.1) * mm, "mid": v(26.98, -27.26) * mm, "end": v(27.22, -27.38) * mm});
            skArc(sketch, "E54.15.13", {"start": v(31.4, -27.17) * mm, "mid": v(31.48, -26.98) * mm, "end": v(31.5, -26.77) * mm});
            skArc(sketch, "E54.15.14", {"start": v(30.39, -23.76) * mm, "mid": v(30.24, -23.54) * mm, "end": v(30.06, -23.36) * mm});
            skArc(sketch, "E54.15.15", {"start": v(30.34, -28.08) * mm, "mid": v(30.55, -28.04) * mm, "end": v(30.73, -27.93) * mm});
            skArc(sketch, "E54.16.0", {"start": v(31.46, -18.61) * mm, "mid": v(30.33, -18.5) * mm, "end": v(29.42, -19.18) * mm});
            skArc(sketch, "E54.16.1", {"start": v(32.87, -12.18) * mm, "mid": v(32.9, -13.31) * mm, "end": v(33.67, -14.14) * mm});
            skLineSegment(sketch, "E54.16.2", {"start": v(32.8, -19.27) * mm, "end": v(31.46, -18.61) * mm});
            skLineSegment(sketch, "E54.16.3", {"start": v(35, -14.8) * mm, "end": v(33.67, -14.14) * mm});
            skPoint(sketch, "E54.16.4", {"position": v(36.71, -19.23) * mm});
            skPoint(sketch, "E54.16.5", {"position": v(37.36, -17.93) * mm});
            skArc(sketch, "E54.16.6", {"start": v(35.42, -15.1) * mm, "mid": v(36.45, -16.33) * mm, "end": v(37.26, -17.72) * mm});
            skPoint(sketch, "E54.16.7", {"position": v(35.22, -14.9) * mm});
            skPoint(sketch, "E54.16.8", {"position": v(33.02, -19.38) * mm});
            skArc(sketch, "E54.16.9", {"start": v(33.3, -19.42) * mm, "mid": v(34.9, -19.49) * mm, "end": v(36.49, -19.28) * mm});
            skLineSegment(sketch, "E54.16.10", {"start": v(36.82, -19.04) * mm, "end": v(37.08, -18.6) * mm});
            skLineSegment(sketch, "E54.16.11", {"start": v(37.27, -18.13) * mm, "end": v(37.08, -18.6) * mm});
            skArc(sketch, "E54.16.12", {"start": v(32.8, -19.27) * mm, "mid": v(33.03, -19.36) * mm, "end": v(33.3, -19.42) * mm});
            skArc(sketch, "E54.16.13", {"start": v(37.27, -18.13) * mm, "mid": v(37.3, -17.92) * mm, "end": v(37.26, -17.72) * mm});
            skArc(sketch, "E54.16.14", {"start": v(35.42, -15.1) * mm, "mid": v(35.22, -14.93) * mm, "end": v(35, -14.8) * mm});
            skArc(sketch, "E54.16.15", {"start": v(36.49, -19.28) * mm, "mid": v(36.68, -19.2) * mm, "end": v(36.82, -19.04) * mm});
            skArc(sketch, "E54.17.0", {"start": v(35.12, -9.85) * mm, "mid": v(34, -10.04) * mm, "end": v(33.3, -10.93) * mm});
            skArc(sketch, "E54.17.1", {"start": v(34.82, -3.27) * mm, "mid": v(35.14, -4.36) * mm, "end": v(36.1, -4.96) * mm});
            skLineSegment(sketch, "E54.17.2", {"start": v(36.58, -10.14) * mm, "end": v(35.12, -9.85) * mm});
            skLineSegment(sketch, "E54.17.3", {"start": v(37.55, -5.25) * mm, "end": v(36.1, -4.96) * mm});
            skPoint(sketch, "E54.17.4", {"position": v(40.35, -9.1) * mm});
            skPoint(sketch, "E54.17.5", {"position": v(40.64, -7.66) * mm});
            skArc(sketch, "E54.17.6", {"start": v(38.04, -5.44) * mm, "mid": v(39.35, -6.36) * mm, "end": v(40.5, -7.49) * mm});
            skPoint(sketch, "E54.17.7", {"position": v(37.8, -5.3) * mm});
            skPoint(sketch, "E54.17.8", {"position": v(36.82, -10.19) * mm});
            skArc(sketch, "E54.17.9", {"start": v(37.1, -10.16) * mm, "mid": v(38.67, -9.8) * mm, "end": v(40.15, -9.2) * mm});
            skLineSegment(sketch, "E54.17.10", {"start": v(40.41, -8.88) * mm, "end": v(40.54, -8.39) * mm});
            skLineSegment(sketch, "E54.17.11", {"start": v(40.61, -7.88) * mm, "end": v(40.54, -8.39) * mm});
            skArc(sketch, "E54.17.12", {"start": v(36.58, -10.14) * mm, "mid": v(36.84, -10.17) * mm, "end": v(37.1, -10.16) * mm});
            skArc(sketch, "E54.17.13", {"start": v(40.61, -7.88) * mm, "mid": v(40.6, -7.67) * mm, "end": v(40.5, -7.49) * mm});
            skArc(sketch, "E54.17.14", {"start": v(38.04, -5.44) * mm, "mid": v(37.8, -5.32) * mm, "end": v(37.55, -5.25) * mm});
            skArc(sketch, "E54.17.15", {"start": v(40.15, -9.2) * mm, "mid": v(40.32, -9.07) * mm, "end": v(40.41, -8.88) * mm});
            skArc(sketch, "E54.18.0", {"start": v(36.4, -0.44) * mm, "mid": v(35.36, -0.91) * mm, "end": v(34.9, -1.95) * mm});
            skArc(sketch, "E54.18.1", {"start": v(34.4, 5.84) * mm, "mid": v(34.98, 4.87) * mm, "end": v(36.06, 4.53) * mm});
            skLineSegment(sketch, "E54.18.2", {"start": v(37.87, -0.34) * mm, "end": v(36.4, -0.44) * mm});
            skLineSegment(sketch, "E54.18.3", {"start": v(37.54, 4.63) * mm, "end": v(36.06, 4.53) * mm});
            skPoint(sketch, "E54.18.4", {"position": v(41.25, 1.64) * mm});
            skPoint(sketch, "E54.18.5", {"position": v(41.15, 3.1) * mm});
            skArc(sketch, "E54.18.6", {"start": v(38.06, 4.58) * mm, "mid": v(39.57, 4.03) * mm, "end": v(40.97, 3.23) * mm});
            skPoint(sketch, "E54.18.7", {"position": v(37.8, 4.65) * mm});
            skPoint(sketch, "E54.18.8", {"position": v(38.12, -0.33) * mm});
            skArc(sketch, "E54.18.9", {"start": v(38.38, -0.22) * mm, "mid": v(39.8, 0.52) * mm, "end": v(41.08, 1.49) * mm});
            skLineSegment(sketch, "E54.18.10", {"start": v(41.25, 1.87) * mm, "end": v(41.25, 2.37) * mm});
            skLineSegment(sketch, "E54.18.11", {"start": v(41.18, 2.88) * mm, "end": v(41.25, 2.37) * mm});
            skArc(sketch, "E54.18.12", {"start": v(37.87, -0.34) * mm, "mid": v(38.13, -0.3) * mm, "end": v(38.38, -0.22) * mm});
            skArc(sketch, "E54.18.13", {"start": v(41.18, 2.88) * mm, "mid": v(41.11, 3.08) * mm, "end": v(40.97, 3.23) * mm});
            skArc(sketch, "E54.18.14", {"start": v(38.06, 4.58) * mm, "mid": v(37.8, 4.62) * mm, "end": v(37.54, 4.63) * mm});
            skArc(sketch, "E54.18.15", {"start": v(41.08, 1.49) * mm, "mid": v(41.2, 1.66) * mm, "end": v(41.25, 1.87) * mm});
            skArc(sketch, "E54.19.0", {"start": v(35.18, 8.98) * mm, "mid": v(34.3, 8.25) * mm, "end": v(34.14, 7.13) * mm});
            skArc(sketch, "E54.19.1", {"start": v(31.63, 14.52) * mm, "mid": v(32.45, 13.74) * mm, "end": v(33.58, 13.7) * mm});
            skLineSegment(sketch, "E54.19.2", {"start": v(36.58, 9.45) * mm, "end": v(35.18, 8.98) * mm});
            skLineSegment(sketch, "E54.19.3", {"start": v(34.98, 14.17) * mm, "end": v(33.58, 13.7) * mm});
            skPoint(sketch, "E54.19.4", {"position": v(39.33, 12.25) * mm});
            skPoint(sketch, "E54.19.5", {"position": v(38.87, 13.63) * mm});
            skArc(sketch, "E54.19.6", {"start": v(35.5, 14.26) * mm, "mid": v(37.1, 14.11) * mm, "end": v(38.65, 13.7) * mm});
            skPoint(sketch, "E54.19.7", {"position": v(35.22, 14.25) * mm});
            skPoint(sketch, "E54.19.8", {"position": v(36.82, 9.53) * mm});
            skArc(sketch, "E54.19.9", {"start": v(37.04, 9.7) * mm, "mid": v(38.23, 10.78) * mm, "end": v(39.21, 12.05) * mm});
            skLineSegment(sketch, "E54.19.10", {"start": v(39.28, 12.46) * mm, "end": v(39.15, 12.95) * mm});
            skLineSegment(sketch, "E54.19.11", {"start": v(38.95, 13.42) * mm, "end": v(39.15, 12.95) * mm});
            skArc(sketch, "E54.19.12", {"start": v(36.58, 9.45) * mm, "mid": v(36.82, 9.56) * mm, "end": v(37.04, 9.7) * mm});
            skArc(sketch, "E54.19.13", {"start": v(38.95, 13.42) * mm, "mid": v(38.83, 13.6) * mm, "end": v(38.65, 13.7) * mm});
            skArc(sketch, "E54.19.14", {"start": v(35.5, 14.26) * mm, "mid": v(35.24, 14.23) * mm, "end": v(34.98, 14.17) * mm});
            skArc(sketch, "E54.19.15", {"start": v(39.21, 12.05) * mm, "mid": v(39.29, 12.25) * mm, "end": v(39.28, 12.46) * mm});
            skArc(sketch, "E54.20.0", {"start": v(31.57, 17.76) * mm, "mid": v(30.92, 16.83) * mm, "end": v(31.05, 15.7) * mm});
            skArc(sketch, "E54.20.1", {"start": v(26.71, 22.2) * mm, "mid": v(27.7, 21.65) * mm, "end": v(28.8, 21.9) * mm});
            skLineSegment(sketch, "E54.20.2", {"start": v(32.8, 18.58) * mm, "end": v(31.57, 17.76) * mm});
            skLineSegment(sketch, "E54.20.3", {"start": v(30.04, 22.73) * mm, "end": v(28.8, 21.9) * mm});
            skPoint(sketch, "E54.20.4", {"position": v(34.74, 22) * mm});
            skPoint(sketch, "E54.20.5", {"position": v(33.93, 23.2) * mm});
            skArc(sketch, "E54.20.6", {"start": v(30.51, 22.94) * mm, "mid": v(32.1, 23.22) * mm, "end": v(33.7, 23.23) * mm});
            skPoint(sketch, "E54.20.7", {"position": v(30.25, 22.87) * mm});
            skPoint(sketch, "E54.20.8", {"position": v(33.02, 18.72) * mm});
            skArc(sketch, "E54.20.9", {"start": v(33.19, 18.94) * mm, "mid": v(34.05, 20.3) * mm, "end": v(34.67, 21.78) * mm});
            skLineSegment(sketch, "E54.20.10", {"start": v(34.63, 22.19) * mm, "end": v(34.37, 22.63) * mm});
            skLineSegment(sketch, "E54.20.11", {"start": v(34.07, 23.03) * mm, "end": v(34.37, 22.63) * mm});
            skArc(sketch, "E54.20.12", {"start": v(32.8, 18.58) * mm, "mid": v(33.01, 18.74) * mm, "end": v(33.19, 18.94) * mm});
            skArc(sketch, "E54.20.13", {"start": v(34.07, 23.03) * mm, "mid": v(33.9, 23.17) * mm, "end": v(33.7, 23.23) * mm});
            skArc(sketch, "E54.20.14", {"start": v(30.51, 22.94) * mm, "mid": v(30.27, 22.85) * mm, "end": v(30.04, 22.73) * mm});
            skArc(sketch, "E54.20.15", {"start": v(34.67, 21.78) * mm, "mid": v(34.7, 21.99) * mm, "end": v(34.63, 22.19) * mm});
            skArc(sketch, "E54.21.0", {"start": v(25.82, 25.3) * mm, "mid": v(25.42, 24.25) * mm, "end": v(25.84, 23.2) * mm});
            skArc(sketch, "E54.21.1", {"start": v(19.97, 28.34) * mm, "mid": v(21.07, 28.07) * mm, "end": v(22.07, 28.6) * mm});
            skLineSegment(sketch, "E54.21.2", {"start": v(26.8, 26.42) * mm, "end": v(25.82, 25.3) * mm});
            skLineSegment(sketch, "E54.21.3", {"start": v(23.05, 29.7) * mm, "end": v(22.07, 28.6) * mm});
            skPoint(sketch, "E54.21.4", {"position": v(27.78, 30.22) * mm});
            skPoint(sketch, "E54.21.5", {"position": v(26.68, 31.18) * mm});
            skArc(sketch, "E54.21.6", {"start": v(23.45, 30.04) * mm, "mid": v(24.9, 30.72) * mm, "end": v(26.46, 31.14) * mm});
            skPoint(sketch, "E54.21.7", {"position": v(23.22, 29.9) * mm});
            skPoint(sketch, "E54.21.8", {"position": v(26.96, 26.61) * mm});
            skArc(sketch, "E54.21.9", {"start": v(27.07, 26.87) * mm, "mid": v(27.55, 28.4) * mm, "end": v(27.77, 30) * mm});
            skLineSegment(sketch, "E54.21.10", {"start": v(27.62, 30.38) * mm, "end": v(27.26, 30.74) * mm});
            skLineSegment(sketch, "E54.21.11", {"start": v(26.86, 31.04) * mm, "end": v(27.26, 30.74) * mm});
            skArc(sketch, "E54.21.12", {"start": v(26.8, 26.42) * mm, "mid": v(26.95, 26.63) * mm, "end": v(27.07, 26.87) * mm});
            skArc(sketch, "E54.21.13", {"start": v(26.86, 31.04) * mm, "mid": v(26.67, 31.14) * mm, "end": v(26.46, 31.14) * mm});
            skArc(sketch, "E54.21.14", {"start": v(23.45, 30.04) * mm, "mid": v(23.24, 29.9) * mm, "end": v(23.05, 29.7) * mm});
            skArc(sketch, "E54.21.15", {"start": v(27.77, 30) * mm, "mid": v(27.74, 30.2) * mm, "end": v(27.62, 30.38) * mm});
            skArc(sketch, "E54.22.0", {"start": v(18.3, 31.11) * mm, "mid": v(18.2, 29.98) * mm, "end": v(18.87, 29.07) * mm});
            skArc(sketch, "E54.22.1", {"start": v(11.87, 32.53) * mm, "mid": v(13, 32.55) * mm, "end": v(13.83, 33.32) * mm});
            skLineSegment(sketch, "E54.22.2", {"start": v(18.96, 32.44) * mm, "end": v(18.3, 31.11) * mm});
            skLineSegment(sketch, "E54.22.3", {"start": v(14.5, 34.65) * mm, "end": v(13.83, 33.32) * mm});
            skPoint(sketch, "E54.22.4", {"position": v(18.93, 36.36) * mm});
            skPoint(sketch, "E54.22.5", {"position": v(17.62, 37) * mm});
            skArc(sketch, "E54.22.6", {"start": v(14.8, 35.07) * mm, "mid": v(16.03, 36.1) * mm, "end": v(17.41, 36.91) * mm});
            skPoint(sketch, "E54.22.7", {"position": v(14.6, 34.87) * mm});
            skPoint(sketch, "E54.22.8", {"position": v(19.07, 32.67) * mm});
            skArc(sketch, "E54.22.9", {"start": v(19.11, 32.94) * mm, "mid": v(19.18, 34.55) * mm, "end": v(18.98, 36.14) * mm});
            skLineSegment(sketch, "E54.22.10", {"start": v(18.74, 36.47) * mm, "end": v(18.3, 36.73) * mm});
            skLineSegment(sketch, "E54.22.11", {"start": v(17.83, 36.92) * mm, "end": v(18.3, 36.73) * mm});
            skArc(sketch, "E54.22.12", {"start": v(18.96, 32.44) * mm, "mid": v(19.06, 32.69) * mm, "end": v(19.11, 32.94) * mm});
            skArc(sketch, "E54.22.13", {"start": v(17.83, 36.92) * mm, "mid": v(17.62, 36.96) * mm, "end": v(17.41, 36.91) * mm});
            skArc(sketch, "E54.22.14", {"start": v(14.8, 35.07) * mm, "mid": v(14.63, 34.87) * mm, "end": v(14.5, 34.65) * mm});
            skArc(sketch, "E54.22.15", {"start": v(18.98, 36.14) * mm, "mid": v(18.9, 36.33) * mm, "end": v(18.74, 36.47) * mm});
            skArc(sketch, "E54.23.0", {"start": v(9.54, 34.77) * mm, "mid": v(9.73, 33.66) * mm, "end": v(10.62, 32.95) * mm});
            skArc(sketch, "E54.23.1", {"start": v(2.97, 34.47) * mm, "mid": v(4.05, 34.79) * mm, "end": v(4.66, 35.74) * mm});
            skLineSegment(sketch, "E54.23.2", {"start": v(9.83, 36.23) * mm, "end": v(9.54, 34.77) * mm});
            skLineSegment(sketch, "E54.23.3", {"start": v(4.95, 37.2) * mm, "end": v(4.66, 35.74) * mm});
            skPoint(sketch, "E54.23.4", {"position": v(8.79, 40) * mm});
            skPoint(sketch, "E54.23.5", {"position": v(7.36, 40.29) * mm});
            skArc(sketch, "E54.23.6", {"start": v(5.13, 37.69) * mm, "mid": v(6.05, 39) * mm, "end": v(7.18, 40.14) * mm});
            skPoint(sketch, "E54.23.7", {"position": v(5, 37.45) * mm});
            skPoint(sketch, "E54.23.8", {"position": v(9.88, 36.47) * mm});
            skArc(sketch, "E54.23.9", {"start": v(9.85, 36.75) * mm, "mid": v(9.5, 38.32) * mm, "end": v(8.9, 39.8) * mm});
            skLineSegment(sketch, "E54.23.10", {"start": v(8.57, 40.06) * mm, "end": v(8.08, 40.2) * mm});
            skLineSegment(sketch, "E54.23.11", {"start": v(7.58, 40.26) * mm, "end": v(8.08, 40.2) * mm});
            skArc(sketch, "E54.23.12", {"start": v(9.83, 36.23) * mm, "mid": v(9.86, 36.49) * mm, "end": v(9.85, 36.75) * mm});
            skArc(sketch, "E54.23.13", {"start": v(7.58, 40.26) * mm, "mid": v(7.37, 40.24) * mm, "end": v(7.18, 40.14) * mm});
            skArc(sketch, "E54.23.14", {"start": v(5.13, 37.69) * mm, "mid": v(5.02, 37.45) * mm, "end": v(4.95, 37.2) * mm});
            skArc(sketch, "E54.23.15", {"start": v(8.9, 39.8) * mm, "mid": v(8.76, 39.97) * mm, "end": v(8.57, 40.06) * mm});
            skArc(sketch, "E55.trimOffspring", {"start": v(-14.83, 31.28) * mm, "mid": v(-15.43, 31) * mm, "end": v(-16.02, 30.7) * mm});
            skArc(sketch, "E56.trimOffspring", {"start": v(-22.5, 26.36) * mm, "mid": v(-23, 25.93) * mm, "end": v(-23.5, 25.49) * mm});
            skArc(sketch, "E57.trimOffspring", {"start": v(-28.64, 19.62) * mm, "mid": v(-29.02, 19.08) * mm, "end": v(-29.38, 18.52) * mm});
            skArc(sketch, "E58.trimOffspring", {"start": v(-32.83, 11.52) * mm, "mid": v(-33.05, 10.9) * mm, "end": v(-33.26, 10.27) * mm});
            skArc(sketch, "E59.trimOffspring", {"start": v(-34.78, 2.62) * mm, "mid": v(-34.83, 1.96) * mm, "end": v(-34.87, 1.3) * mm});
            skArc(sketch, "E60.trimOffspring", {"start": v(-34.36, -6.5) * mm, "mid": v(-34.23, -7.14) * mm, "end": v(-34.1, -7.79) * mm});
            skArc(sketch, "E61.trimOffspring", {"start": v(-31.59, -15.18) * mm, "mid": v(-31.3, -15.77) * mm, "end": v(-31, -16.37) * mm});
            skArc(sketch, "E62.trimOffspring", {"start": v(-26.67, -22.85) * mm, "mid": v(-26.24, -23.36) * mm, "end": v(-25.8, -23.85) * mm});
            skArc(sketch, "E63.trimOffspring", {"start": v(-19.93, -29) * mm, "mid": v(-19.38, -29.37) * mm, "end": v(-18.83, -29.73) * mm});
            skArc(sketch, "E64.trimOffspring", {"start": v(-11.83, -33.18) * mm, "mid": v(-11.2, -33.4) * mm, "end": v(-10.58, -33.6) * mm});
            skArc(sketch, "E65.trimOffspring", {"start": v(-2.92, -35.13) * mm, "mid": v(-2.26, -35.18) * mm, "end": v(-1.6, -35.22) * mm});
            skArc(sketch, "E66.trimOffspring", {"start": v(6.19, -34.7) * mm, "mid": v(6.84, -34.58) * mm, "end": v(7.48, -34.45) * mm});
            skArc(sketch, "E67.trimOffspring", {"start": v(14.87, -31.94) * mm, "mid": v(15.47, -31.65) * mm, "end": v(16.06, -31.35) * mm});
            skArc(sketch, "E68.trimOffspring", {"start": v(22.55, -27.02) * mm, "mid": v(23.05, -26.59) * mm, "end": v(23.54, -26.15) * mm});
            skArc(sketch, "E69.trimOffspring", {"start": v(28.69, -20.28) * mm, "mid": v(29.06, -19.73) * mm, "end": v(29.42, -19.18) * mm});
            skArc(sketch, "E70.trimOffspring", {"start": v(32.87, -12.18) * mm, "mid": v(33.1, -11.55) * mm, "end": v(33.3, -10.93) * mm});
            skArc(sketch, "E71.trimOffspring", {"start": v(34.82, -3.27) * mm, "mid": v(34.87, -2.61) * mm, "end": v(34.9, -1.95) * mm});
            skArc(sketch, "E72.trimOffspring", {"start": v(34.4, 5.84) * mm, "mid": v(34.28, 6.49) * mm, "end": v(34.14, 7.13) * mm});
            skArc(sketch, "E73.trimOffspring", {"start": v(31.63, 14.52) * mm, "mid": v(31.34, 15.12) * mm, "end": v(31.05, 15.7) * mm});
            skArc(sketch, "E74.trimOffspring", {"start": v(26.71, 22.2) * mm, "mid": v(26.28, 22.7) * mm, "end": v(25.84, 23.2) * mm});
            skArc(sketch, "E75.trimOffspring", {"start": v(19.97, 28.34) * mm, "mid": v(19.42, 28.71) * mm, "end": v(18.87, 29.07) * mm});
            skArc(sketch, "E76.trimOffspring", {"start": v(11.87, 32.53) * mm, "mid": v(11.25, 32.74) * mm, "end": v(10.62, 32.95) * mm});
            skArc(sketch, "E77.trimOffspring", {"start": v(2.97, 34.47) * mm, "mid": v(2.3, 34.52) * mm, "end": v(1.65, 34.56) * mm});
            skSolve(sketch);
        }
        {
            var Q0;
            Q0=qSketchRegion(id+"F0",true);
            var Q1;
            Q1=makeQuery(id+"F2.imprint","IMPRINT",FACE,{"disambiguationData":[TD([[makeQuery(id+"F2.imprint","IMPRINT",EDGE,{"derivedFrom":sQuery(id+"F2.wireOp",EDGE,"E39")}),1.0]])]});
            var Q2;
            Q2=sQuery(id+"F0.wireOp",VERTEX,"E15.1.11.end");
            var Q3;
            Q3=sQuery(id+"F2.wireOp",VERTEX,"E54.2.11.end");
            loft(context, id + "F3", {"sheetProfilesArray" : [{ "sheetProfileEntities" : qUnion([Q0]) }, { "sheetProfileEntities" : qUnion([Q1]) }], "matchConnections" : true, "connections" : [{ "connectionEntities" : qUnion([Q2, Q3]), "connectionEdgeQueries" : qUnion([]), "connectionEdgeParameters" : [] }]});
        }
        {
            var Q0;
            Q0=sQuery(id+"F2.wireOp",VERTEX,"E39.center");
            var Q1;
            Q1=makeQuery(id+"F3.opLoft","SWEPT_BODY",BODY,{"disambiguationData":[OSD([makeQuery(id+"F0.imprint","IMPRINT",FACE,{"disambiguationData":[TD([[makeQuery(id+"F0.imprint","IMPRINT",EDGE,{"derivedFrom":sQuery(id+"F0.wireOp",EDGE,"E0")}),1.0]])]}),makeQuery(id+"F2.imprint","IMPRINT",FACE,{"disambiguationData":[TD([[makeQuery(id+"F2.imprint","IMPRINT",EDGE,{"derivedFrom":sQuery(id+"F2.wireOp",EDGE,"E39")}),1.0]])]})])]});
            hole(context, id + "F4", {"style" : HoleStyle.SIMPLE, "endStyle" : HoleEndStyle.BLIND, "holeDiameter" : 12.7 * mm, "holeDepth" : 50.8 * mm, "tappedDepth" : 12.7 * mm, "tapClearance" : 3, "locations" : qUnion([Q0]), "scope" : qUnion([Q1])});
        }
    });
